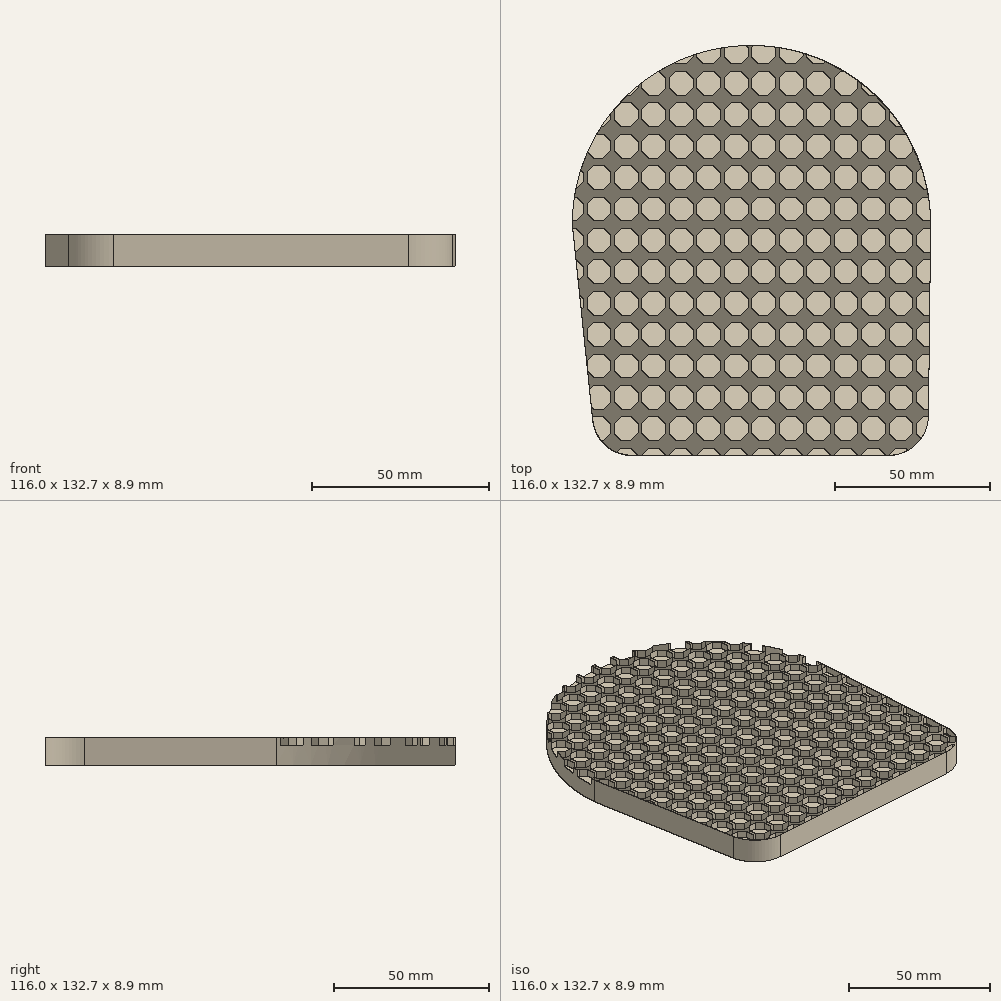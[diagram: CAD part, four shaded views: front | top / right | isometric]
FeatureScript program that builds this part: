
annotation { "Feature Type Name" : "Feature", "Feature Type Description" : "" }
export const myFeature = defineFeature(function(context is Context, id is Id, definition is map)
    precondition{}
    {
        {
            var Q0;
            Q0=qCreatedBy(makeId("Top.planeOp"),FACE);
            var sketch = newSketch(context, id + "F0", { "sketchPlane" : qUnion([Q0])});
            skLineSegment(sketch, "E0.0", {"start": v(-38.75, -61.92) * mm, "end": v(44.57, -61.92) * mm});
            skArc(sketch, "E1", {"start": v(57.99, 12.79) * mm, "mid": v(0, 70.77) * mm, "end": v(-57.99, 12.79) * mm});
            skLineSegment(sketch, "E2", {"start": v(-57.99, 12.79) * mm, "end": v(-51.38, -50.53) * mm});
            skLineSegment(sketch, "E3", {"start": v(57.99, 12.79) * mm, "end": v(57.27, -49.36) * mm});
            skArc(sketch, "E4.filletArc", {"start": v(-51.38, -50.53) * mm, "mid": v(-47.25, -58.65) * mm, "end": v(-38.75, -61.92) * mm});
            skArc(sketch, "E5.filletArc", {"start": v(44.57, -61.92) * mm, "mid": v(53.5, -58.25) * mm, "end": v(57.27, -49.36) * mm});
            skPoint(sketch, "E6.endSnap0", {"position": v(0, 70.77) * mm});
            skSolve(sketch);
        }
        {
            var Q0;
            Q0 = qSketchRegion(id + "F0", true);
            var Q1;
            Q1=makeQuery(id+"F0.imprint","IMPRINT",FACE,{"disambiguationData":[TD([[makeQuery(id+"F0.imprint","IMPRINT",EDGE,{"derivedFrom":sQuery(id+"F0.wireOp",EDGE,"E0.0")}),1.0]])]});
            extrude(context, id + "F1", {"entities" : qUnion([Q0, Q1]), "depth" : 6.35 * mm, "offsetDistance" : 25.4 * mm});
        }
        {
            var Q0;
            Q0=makeQuery(id+"F0.imprint","IMPRINT",FACE,{"disambiguationData":[TD([[makeQuery(id+"F0.imprint","IMPRINT",EDGE,{"derivedFrom":sQuery(id+"F0.wireOp",EDGE,"E0.0")}),1.0]])]});
            var sketch = newSketch(context, id + "F2", { "sketchPlane" : qUnion([Q0])});
            skLineSegment(sketch, "E7.1.5.2", {"start": v(-55.62, -9.87) * mm, "end": v(-54.45, -11.04) * mm});
            skLineSegment(sketch, "E7.1.5.4", {"start": v(-55.1, -14.87) * mm, "end": v(-54.45, -14.22) * mm});
            skLineSegment(sketch, "E7.1.5.5", {"start": v(-54.45, -14.22) * mm, "end": v(-54.45, -11.04) * mm});
            skLineSegment(sketch, "E7.1.6.2", {"start": v(-56.7, 1.36) * mm, "end": v(-54.45, -0.88) * mm});
            skLineSegment(sketch, "E7.1.6.3", {"start": v(-56.8, 1.36) * mm, "end": v(-56.7, 1.36) * mm});
            skLineSegment(sketch, "E7.1.6.4", {"start": v(-56.06, -5.67) * mm, "end": v(-54.45, -4.06) * mm});
            skLineSegment(sketch, "E7.1.6.5", {"start": v(-54.45, -4.06) * mm, "end": v(-54.45, -0.88) * mm});
            skLineSegment(sketch, "E7.1.7.0", {"start": v(-57.05, 3.86) * mm, "end": v(-56.7, 3.86) * mm});
            skLineSegment(sketch, "E7.1.7.2", {"start": v(-56.7, 11.52) * mm, "end": v(-54.45, 9.28) * mm});
            skLineSegment(sketch, "E7.1.7.3", {"start": v(-57.85, 11.52) * mm, "end": v(-56.7, 11.52) * mm});
            skLineSegment(sketch, "E7.1.7.4", {"start": v(-56.7, 3.86) * mm, "end": v(-54.45, 6.1) * mm});
            skLineSegment(sketch, "E7.1.7.5", {"start": v(-54.45, 6.1) * mm, "end": v(-54.45, 9.28) * mm});
            skLineSegment(sketch, "E7.1.8.0", {"start": v(-57.98, 14.02) * mm, "end": v(-56.7, 14.02) * mm});
            skLineSegment(sketch, "E7.1.8.2", {"start": v(-56.7, 21.68) * mm, "end": v(-54.45, 19.44) * mm});
            skLineSegment(sketch, "E7.1.8.3", {"start": v(-57.32, 21.68) * mm, "end": v(-56.7, 21.68) * mm});
            skLineSegment(sketch, "E7.1.8.4", {"start": v(-56.7, 14.02) * mm, "end": v(-54.45, 16.26) * mm});
            skLineSegment(sketch, "E7.1.8.5", {"start": v(-54.45, 16.26) * mm, "end": v(-54.45, 19.44) * mm});
            skLineSegment(sketch, "E7.1.9.0", {"start": v(-56.88, 24.18) * mm, "end": v(-56.7, 24.18) * mm});
            skLineSegment(sketch, "E7.1.9.2", {"start": v(-55.27, 30.42) * mm, "end": v(-54.45, 29.6) * mm});
            skLineSegment(sketch, "E7.1.9.4", {"start": v(-56.7, 24.18) * mm, "end": v(-54.45, 26.42) * mm});
            skLineSegment(sketch, "E7.1.9.5", {"start": v(-54.45, 26.42) * mm, "end": v(-54.45, 29.6) * mm});
            skLineSegment(sketch, "E7.2.1.0", {"start": v(-48.65, -57.1) * mm, "end": v(-47.8, -57.1) * mm});
            skLineSegment(sketch, "E7.2.1.1", {"start": v(-51.45, -49.9) * mm, "end": v(-50.98, -49.44) * mm});
            skLineSegment(sketch, "E7.2.1.2", {"start": v(-47.8, -49.44) * mm, "end": v(-45.56, -51.68) * mm});
            skLineSegment(sketch, "E7.2.1.3", {"start": v(-50.98, -49.44) * mm, "end": v(-47.8, -49.44) * mm});
            skLineSegment(sketch, "E7.2.1.4", {"start": v(-47.8, -57.1) * mm, "end": v(-45.56, -54.86) * mm});
            skLineSegment(sketch, "E7.2.1.5", {"start": v(-45.56, -54.86) * mm, "end": v(-45.56, -51.68) * mm});
            skLineSegment(sketch, "E7.2.2.0", {"start": v(-50.98, -46.94) * mm, "end": v(-47.8, -46.94) * mm});
            skLineSegment(sketch, "E7.2.2.1", {"start": v(-52.4, -40.7) * mm, "end": v(-50.98, -39.28) * mm});
            skLineSegment(sketch, "E7.2.2.2", {"start": v(-47.8, -39.28) * mm, "end": v(-45.56, -41.52) * mm});
            skLineSegment(sketch, "E7.2.2.3", {"start": v(-50.98, -39.28) * mm, "end": v(-47.8, -39.28) * mm});
            skLineSegment(sketch, "E7.2.2.4", {"start": v(-47.8, -46.94) * mm, "end": v(-45.56, -44.7) * mm});
            skLineSegment(sketch, "E7.2.2.5", {"start": v(-45.56, -44.7) * mm, "end": v(-45.56, -41.52) * mm});
            skLineSegment(sketch, "E7.2.2.6", {"start": v(-51.84, -46.07) * mm, "end": v(-50.98, -46.94) * mm});
            skLineSegment(sketch, "E7.2.3.0", {"start": v(-50.98, -36.78) * mm, "end": v(-47.8, -36.78) * mm});
            skLineSegment(sketch, "E7.2.3.1", {"start": v(-53.22, -31.36) * mm, "end": v(-50.98, -29.12) * mm});
            skLineSegment(sketch, "E7.2.3.2", {"start": v(-47.8, -29.12) * mm, "end": v(-45.56, -31.36) * mm});
            skLineSegment(sketch, "E7.2.3.3", {"start": v(-50.98, -29.12) * mm, "end": v(-47.8, -29.12) * mm});
            skLineSegment(sketch, "E7.2.3.4", {"start": v(-47.8, -36.78) * mm, "end": v(-45.56, -34.54) * mm});
            skLineSegment(sketch, "E7.2.3.5", {"start": v(-45.56, -34.54) * mm, "end": v(-45.56, -31.36) * mm});
            skLineSegment(sketch, "E7.2.3.6", {"start": v(-53.03, -34.73) * mm, "end": v(-50.98, -36.78) * mm});
            skLineSegment(sketch, "E7.2.3.7", {"start": v(-53.22, -32.86) * mm, "end": v(-53.22, -31.36) * mm});
            skLineSegment(sketch, "E7.2.4.0", {"start": v(-50.98, -26.62) * mm, "end": v(-47.8, -26.62) * mm});
            skLineSegment(sketch, "E7.2.4.1", {"start": v(-53.22, -21.2) * mm, "end": v(-50.98, -18.96) * mm});
            skLineSegment(sketch, "E7.2.4.2", {"start": v(-47.8, -18.96) * mm, "end": v(-45.56, -21.2) * mm});
            skLineSegment(sketch, "E7.2.4.3", {"start": v(-50.98, -18.96) * mm, "end": v(-47.8, -18.96) * mm});
            skLineSegment(sketch, "E7.2.4.4", {"start": v(-47.8, -26.62) * mm, "end": v(-45.56, -24.38) * mm});
            skLineSegment(sketch, "E7.2.4.5", {"start": v(-45.56, -24.38) * mm, "end": v(-45.56, -21.2) * mm});
            skLineSegment(sketch, "E7.2.4.6", {"start": v(-53.22, -24.38) * mm, "end": v(-50.98, -26.62) * mm});
            skLineSegment(sketch, "E7.2.4.7", {"start": v(-53.22, -24.38) * mm, "end": v(-53.22, -21.2) * mm});
            skLineSegment(sketch, "E7.2.5.0", {"start": v(-50.98, -16.46) * mm, "end": v(-47.8, -16.46) * mm});
            skLineSegment(sketch, "E7.2.5.1", {"start": v(-53.22, -11.04) * mm, "end": v(-50.98, -8.8) * mm});
            skLineSegment(sketch, "E7.2.5.2", {"start": v(-47.8, -8.8) * mm, "end": v(-45.56, -11.04) * mm});
            skLineSegment(sketch, "E7.2.5.3", {"start": v(-50.98, -8.8) * mm, "end": v(-47.8, -8.8) * mm});
            skLineSegment(sketch, "E7.2.5.4", {"start": v(-47.8, -16.46) * mm, "end": v(-45.56, -14.22) * mm});
            skLineSegment(sketch, "E7.2.5.5", {"start": v(-45.56, -14.22) * mm, "end": v(-45.56, -11.04) * mm});
            skLineSegment(sketch, "E7.2.5.6", {"start": v(-53.22, -14.22) * mm, "end": v(-50.98, -16.46) * mm});
            skLineSegment(sketch, "E7.2.5.7", {"start": v(-53.22, -14.22) * mm, "end": v(-53.22, -11.04) * mm});
            skLineSegment(sketch, "E7.2.6.0", {"start": v(-50.98, -6.3) * mm, "end": v(-47.8, -6.3) * mm});
            skLineSegment(sketch, "E7.2.6.1", {"start": v(-53.22, -0.88) * mm, "end": v(-50.98, 1.36) * mm});
            skLineSegment(sketch, "E7.2.6.2", {"start": v(-47.8, 1.36) * mm, "end": v(-45.56, -0.88) * mm});
            skLineSegment(sketch, "E7.2.6.3", {"start": v(-50.98, 1.36) * mm, "end": v(-47.8, 1.36) * mm});
            skLineSegment(sketch, "E7.2.6.4", {"start": v(-47.8, -6.3) * mm, "end": v(-45.56, -4.06) * mm});
            skLineSegment(sketch, "E7.2.6.5", {"start": v(-45.56, -4.06) * mm, "end": v(-45.56, -0.88) * mm});
            skLineSegment(sketch, "E7.2.6.6", {"start": v(-53.22, -4.06) * mm, "end": v(-50.98, -6.3) * mm});
            skLineSegment(sketch, "E7.2.6.7", {"start": v(-53.22, -4.06) * mm, "end": v(-53.22, -0.88) * mm});
            skLineSegment(sketch, "E7.2.7.0", {"start": v(-50.98, 3.86) * mm, "end": v(-47.8, 3.86) * mm});
            skLineSegment(sketch, "E7.2.7.1", {"start": v(-53.22, 9.28) * mm, "end": v(-50.98, 11.52) * mm});
            skLineSegment(sketch, "E7.2.7.2", {"start": v(-47.8, 11.52) * mm, "end": v(-45.56, 9.28) * mm});
            skLineSegment(sketch, "E7.2.7.3", {"start": v(-50.98, 11.52) * mm, "end": v(-47.8, 11.52) * mm});
            skLineSegment(sketch, "E7.2.7.4", {"start": v(-47.8, 3.86) * mm, "end": v(-45.56, 6.1) * mm});
            skLineSegment(sketch, "E7.2.7.5", {"start": v(-45.56, 6.1) * mm, "end": v(-45.56, 9.28) * mm});
            skLineSegment(sketch, "E7.2.7.6", {"start": v(-53.22, 6.1) * mm, "end": v(-50.98, 3.86) * mm});
            skLineSegment(sketch, "E7.2.7.7", {"start": v(-53.22, 6.1) * mm, "end": v(-53.22, 9.28) * mm});
            skLineSegment(sketch, "E7.2.8.0", {"start": v(-50.98, 14.02) * mm, "end": v(-47.8, 14.02) * mm});
            skLineSegment(sketch, "E7.2.8.1", {"start": v(-53.22, 19.44) * mm, "end": v(-50.98, 21.68) * mm});
            skLineSegment(sketch, "E7.2.8.2", {"start": v(-47.8, 21.68) * mm, "end": v(-45.56, 19.44) * mm});
            skLineSegment(sketch, "E7.2.8.3", {"start": v(-50.98, 21.68) * mm, "end": v(-47.8, 21.68) * mm});
            skLineSegment(sketch, "E7.2.8.4", {"start": v(-47.8, 14.02) * mm, "end": v(-45.56, 16.26) * mm});
            skLineSegment(sketch, "E7.2.8.5", {"start": v(-45.56, 16.26) * mm, "end": v(-45.56, 19.44) * mm});
            skLineSegment(sketch, "E7.2.8.6", {"start": v(-53.22, 16.26) * mm, "end": v(-50.98, 14.02) * mm});
            skLineSegment(sketch, "E7.2.8.7", {"start": v(-53.22, 16.26) * mm, "end": v(-53.22, 19.44) * mm});
            skLineSegment(sketch, "E7.2.9.0", {"start": v(-50.98, 24.18) * mm, "end": v(-47.8, 24.18) * mm});
            skLineSegment(sketch, "E7.2.9.1", {"start": v(-53.22, 29.6) * mm, "end": v(-50.98, 31.84) * mm});
            skLineSegment(sketch, "E7.2.9.2", {"start": v(-47.8, 31.84) * mm, "end": v(-45.56, 29.6) * mm});
            skLineSegment(sketch, "E7.2.9.3", {"start": v(-50.98, 31.84) * mm, "end": v(-47.8, 31.84) * mm});
            skLineSegment(sketch, "E7.2.9.4", {"start": v(-47.8, 24.18) * mm, "end": v(-45.56, 26.42) * mm});
            skLineSegment(sketch, "E7.2.9.5", {"start": v(-45.56, 26.42) * mm, "end": v(-45.56, 29.6) * mm});
            skLineSegment(sketch, "E7.2.9.6", {"start": v(-53.22, 26.42) * mm, "end": v(-50.98, 24.18) * mm});
            skLineSegment(sketch, "E7.2.9.7", {"start": v(-53.22, 26.42) * mm, "end": v(-53.22, 29.6) * mm});
            skLineSegment(sketch, "E7.2.10.0", {"start": v(-50.98, 34.34) * mm, "end": v(-47.8, 34.34) * mm});
            skLineSegment(sketch, "E7.2.10.2", {"start": v(-47.8, 42) * mm, "end": v(-45.56, 39.76) * mm});
            skLineSegment(sketch, "E7.2.10.3", {"start": v(-50.14, 42) * mm, "end": v(-47.8, 42) * mm});
            skLineSegment(sketch, "E7.2.10.4", {"start": v(-47.8, 34.34) * mm, "end": v(-45.56, 36.58) * mm});
            skLineSegment(sketch, "E7.2.10.5", {"start": v(-45.56, 36.58) * mm, "end": v(-45.56, 39.76) * mm});
            skLineSegment(sketch, "E7.2.10.6", {"start": v(-53.01, 36.37) * mm, "end": v(-50.98, 34.34) * mm});
            skLineSegment(sketch, "E7.2.11.0", {"start": v(-48.6, 44.5) * mm, "end": v(-47.8, 44.5) * mm});
            skLineSegment(sketch, "E7.2.11.4", {"start": v(-47.8, 44.5) * mm, "end": v(-45.56, 46.74) * mm});
            skLineSegment(sketch, "E7.2.11.5", {"start": v(-45.56, 46.74) * mm, "end": v(-45.56, 48.74) * mm});
            skLineSegment(sketch, "E7.3.0.1", {"start": v(-43.44, -60.95) * mm, "end": v(-42.09, -59.6) * mm});
            skLineSegment(sketch, "E7.3.0.2", {"start": v(-38.91, -59.6) * mm, "end": v(-36.67, -61.84) * mm});
            skLineSegment(sketch, "E7.3.0.3", {"start": v(-42.09, -59.6) * mm, "end": v(-38.91, -59.6) * mm});
            skLineSegment(sketch, "E7.3.1.0", {"start": v(-42.09, -57.1) * mm, "end": v(-38.91, -57.1) * mm});
            skLineSegment(sketch, "E7.3.1.1", {"start": v(-44.33, -51.68) * mm, "end": v(-42.09, -49.44) * mm});
            skLineSegment(sketch, "E7.3.1.2", {"start": v(-38.91, -49.44) * mm, "end": v(-36.67, -51.68) * mm});
            skLineSegment(sketch, "E7.3.1.3", {"start": v(-42.09, -49.44) * mm, "end": v(-38.91, -49.44) * mm});
            skLineSegment(sketch, "E7.3.1.4", {"start": v(-38.91, -57.1) * mm, "end": v(-36.67, -54.86) * mm});
            skLineSegment(sketch, "E7.3.1.5", {"start": v(-36.67, -54.86) * mm, "end": v(-36.67, -51.68) * mm});
            skLineSegment(sketch, "E7.3.1.6", {"start": v(-44.33, -54.86) * mm, "end": v(-42.09, -57.1) * mm});
            skLineSegment(sketch, "E7.3.1.7", {"start": v(-44.33, -54.86) * mm, "end": v(-44.33, -51.68) * mm});
            skLineSegment(sketch, "E7.3.2.0", {"start": v(-42.09, -46.94) * mm, "end": v(-38.91, -46.94) * mm});
            skLineSegment(sketch, "E7.3.2.1", {"start": v(-44.33, -41.52) * mm, "end": v(-42.09, -39.28) * mm});
            skLineSegment(sketch, "E7.3.2.2", {"start": v(-38.91, -39.28) * mm, "end": v(-36.67, -41.52) * mm});
            skLineSegment(sketch, "E7.3.2.3", {"start": v(-42.09, -39.28) * mm, "end": v(-38.91, -39.28) * mm});
            skLineSegment(sketch, "E7.3.2.4", {"start": v(-38.91, -46.94) * mm, "end": v(-36.67, -44.7) * mm});
            skLineSegment(sketch, "E7.3.2.5", {"start": v(-36.67, -44.7) * mm, "end": v(-36.67, -41.52) * mm});
            skLineSegment(sketch, "E7.3.2.6", {"start": v(-44.33, -44.7) * mm, "end": v(-42.09, -46.94) * mm});
            skLineSegment(sketch, "E7.3.2.7", {"start": v(-44.33, -44.7) * mm, "end": v(-44.33, -41.52) * mm});
            skLineSegment(sketch, "E7.3.3.0", {"start": v(-42.09, -36.78) * mm, "end": v(-38.91, -36.78) * mm});
            skLineSegment(sketch, "E7.3.3.1", {"start": v(-44.33, -31.36) * mm, "end": v(-42.09, -29.12) * mm});
            skLineSegment(sketch, "E7.3.3.2", {"start": v(-38.91, -29.12) * mm, "end": v(-36.67, -31.36) * mm});
            skLineSegment(sketch, "E7.3.3.3", {"start": v(-42.09, -29.12) * mm, "end": v(-38.91, -29.12) * mm});
            skLineSegment(sketch, "E7.3.3.4", {"start": v(-38.91, -36.78) * mm, "end": v(-36.67, -34.54) * mm});
            skLineSegment(sketch, "E7.3.3.5", {"start": v(-36.67, -34.54) * mm, "end": v(-36.67, -31.36) * mm});
            skLineSegment(sketch, "E7.3.3.6", {"start": v(-44.33, -34.54) * mm, "end": v(-42.09, -36.78) * mm});
            skLineSegment(sketch, "E7.3.3.7", {"start": v(-44.33, -34.54) * mm, "end": v(-44.33, -31.36) * mm});
            skLineSegment(sketch, "E7.3.4.0", {"start": v(-42.09, -26.62) * mm, "end": v(-38.91, -26.62) * mm});
            skLineSegment(sketch, "E7.3.4.1", {"start": v(-44.33, -21.2) * mm, "end": v(-42.09, -18.96) * mm});
            skLineSegment(sketch, "E7.3.4.2", {"start": v(-38.91, -18.96) * mm, "end": v(-36.67, -21.2) * mm});
            skLineSegment(sketch, "E7.3.4.3", {"start": v(-42.09, -18.96) * mm, "end": v(-38.91, -18.96) * mm});
            skLineSegment(sketch, "E7.3.4.4", {"start": v(-38.91, -26.62) * mm, "end": v(-36.67, -24.38) * mm});
            skLineSegment(sketch, "E7.3.4.5", {"start": v(-36.67, -24.38) * mm, "end": v(-36.67, -21.2) * mm});
            skLineSegment(sketch, "E7.3.4.6", {"start": v(-44.33, -24.38) * mm, "end": v(-42.09, -26.62) * mm});
            skLineSegment(sketch, "E7.3.4.7", {"start": v(-44.33, -24.38) * mm, "end": v(-44.33, -21.2) * mm});
            skLineSegment(sketch, "E7.3.5.0", {"start": v(-42.09, -16.46) * mm, "end": v(-38.91, -16.46) * mm});
            skLineSegment(sketch, "E7.3.5.1", {"start": v(-44.33, -11.04) * mm, "end": v(-42.09, -8.8) * mm});
            skLineSegment(sketch, "E7.3.5.2", {"start": v(-38.91, -8.8) * mm, "end": v(-36.67, -11.04) * mm});
            skLineSegment(sketch, "E7.3.5.3", {"start": v(-42.09, -8.8) * mm, "end": v(-38.91, -8.8) * mm});
            skLineSegment(sketch, "E7.3.5.4", {"start": v(-38.91, -16.46) * mm, "end": v(-36.67, -14.22) * mm});
            skLineSegment(sketch, "E7.3.5.5", {"start": v(-36.67, -14.22) * mm, "end": v(-36.67, -11.04) * mm});
            skLineSegment(sketch, "E7.3.5.6", {"start": v(-44.33, -14.22) * mm, "end": v(-42.09, -16.46) * mm});
            skLineSegment(sketch, "E7.3.5.7", {"start": v(-44.33, -14.22) * mm, "end": v(-44.33, -11.04) * mm});
            skLineSegment(sketch, "E7.3.6.0", {"start": v(-42.09, -6.3) * mm, "end": v(-38.91, -6.3) * mm});
            skLineSegment(sketch, "E7.3.6.1", {"start": v(-44.33, -0.88) * mm, "end": v(-42.09, 1.36) * mm});
            skLineSegment(sketch, "E7.3.6.2", {"start": v(-38.91, 1.36) * mm, "end": v(-36.67, -0.88) * mm});
            skLineSegment(sketch, "E7.3.6.3", {"start": v(-42.09, 1.36) * mm, "end": v(-38.91, 1.36) * mm});
            skLineSegment(sketch, "E7.3.6.4", {"start": v(-38.91, -6.3) * mm, "end": v(-36.67, -4.06) * mm});
            skLineSegment(sketch, "E7.3.6.5", {"start": v(-36.67, -4.06) * mm, "end": v(-36.67, -0.88) * mm});
            skLineSegment(sketch, "E7.3.6.6", {"start": v(-44.33, -4.06) * mm, "end": v(-42.09, -6.3) * mm});
            skLineSegment(sketch, "E7.3.6.7", {"start": v(-44.33, -4.06) * mm, "end": v(-44.33, -0.88) * mm});
            skLineSegment(sketch, "E7.3.7.0", {"start": v(-42.09, 3.86) * mm, "end": v(-38.91, 3.86) * mm});
            skLineSegment(sketch, "E7.3.7.1", {"start": v(-44.33, 9.28) * mm, "end": v(-42.09, 11.52) * mm});
            skLineSegment(sketch, "E7.3.7.2", {"start": v(-38.91, 11.52) * mm, "end": v(-36.67, 9.28) * mm});
            skLineSegment(sketch, "E7.3.7.3", {"start": v(-42.09, 11.52) * mm, "end": v(-38.91, 11.52) * mm});
            skLineSegment(sketch, "E7.3.7.4", {"start": v(-38.91, 3.86) * mm, "end": v(-36.67, 6.1) * mm});
            skLineSegment(sketch, "E7.3.7.5", {"start": v(-36.67, 6.1) * mm, "end": v(-36.67, 9.28) * mm});
            skLineSegment(sketch, "E7.3.7.6", {"start": v(-44.33, 6.1) * mm, "end": v(-42.09, 3.86) * mm});
            skLineSegment(sketch, "E7.3.7.7", {"start": v(-44.33, 6.1) * mm, "end": v(-44.33, 9.28) * mm});
            skLineSegment(sketch, "E7.3.8.0", {"start": v(-42.09, 14.02) * mm, "end": v(-38.91, 14.02) * mm});
            skLineSegment(sketch, "E7.3.8.1", {"start": v(-44.33, 19.44) * mm, "end": v(-42.09, 21.68) * mm});
            skLineSegment(sketch, "E7.3.8.2", {"start": v(-38.91, 21.68) * mm, "end": v(-36.67, 19.44) * mm});
            skLineSegment(sketch, "E7.3.8.3", {"start": v(-42.09, 21.68) * mm, "end": v(-38.91, 21.68) * mm});
            skLineSegment(sketch, "E7.3.8.4", {"start": v(-38.91, 14.02) * mm, "end": v(-36.67, 16.26) * mm});
            skLineSegment(sketch, "E7.3.8.5", {"start": v(-36.67, 16.26) * mm, "end": v(-36.67, 19.44) * mm});
            skLineSegment(sketch, "E7.3.8.6", {"start": v(-44.33, 16.26) * mm, "end": v(-42.09, 14.02) * mm});
            skLineSegment(sketch, "E7.3.8.7", {"start": v(-44.33, 16.26) * mm, "end": v(-44.33, 19.44) * mm});
            skLineSegment(sketch, "E7.3.9.0", {"start": v(-42.09, 24.18) * mm, "end": v(-38.91, 24.18) * mm});
            skLineSegment(sketch, "E7.3.9.1", {"start": v(-44.33, 29.6) * mm, "end": v(-42.09, 31.84) * mm});
            skLineSegment(sketch, "E7.3.9.2", {"start": v(-38.91, 31.84) * mm, "end": v(-36.67, 29.6) * mm});
            skLineSegment(sketch, "E7.3.9.3", {"start": v(-42.09, 31.84) * mm, "end": v(-38.91, 31.84) * mm});
            skLineSegment(sketch, "E7.3.9.4", {"start": v(-38.91, 24.18) * mm, "end": v(-36.67, 26.42) * mm});
            skLineSegment(sketch, "E7.3.9.5", {"start": v(-36.67, 26.42) * mm, "end": v(-36.67, 29.6) * mm});
            skLineSegment(sketch, "E7.3.9.6", {"start": v(-44.33, 26.42) * mm, "end": v(-42.09, 24.18) * mm});
            skLineSegment(sketch, "E7.3.9.7", {"start": v(-44.33, 26.42) * mm, "end": v(-44.33, 29.6) * mm});
            skLineSegment(sketch, "E7.3.10.0", {"start": v(-42.09, 34.34) * mm, "end": v(-38.91, 34.34) * mm});
            skLineSegment(sketch, "E7.3.10.1", {"start": v(-44.33, 39.76) * mm, "end": v(-42.09, 42) * mm});
            skLineSegment(sketch, "E7.3.10.2", {"start": v(-38.91, 42) * mm, "end": v(-36.67, 39.76) * mm});
            skLineSegment(sketch, "E7.3.10.3", {"start": v(-42.09, 42) * mm, "end": v(-38.91, 42) * mm});
            skLineSegment(sketch, "E7.3.10.4", {"start": v(-38.91, 34.34) * mm, "end": v(-36.67, 36.58) * mm});
            skLineSegment(sketch, "E7.3.10.5", {"start": v(-36.67, 36.58) * mm, "end": v(-36.67, 39.76) * mm});
            skLineSegment(sketch, "E7.3.10.6", {"start": v(-44.33, 36.58) * mm, "end": v(-42.09, 34.34) * mm});
            skLineSegment(sketch, "E7.3.10.7", {"start": v(-44.33, 36.58) * mm, "end": v(-44.33, 39.76) * mm});
            skLineSegment(sketch, "E7.3.11.0", {"start": v(-42.09, 44.5) * mm, "end": v(-38.91, 44.5) * mm});
            skLineSegment(sketch, "E7.3.11.1", {"start": v(-44.33, 49.92) * mm, "end": v(-42.09, 52.16) * mm});
            skLineSegment(sketch, "E7.3.11.2", {"start": v(-38.91, 52.16) * mm, "end": v(-36.67, 49.92) * mm});
            skLineSegment(sketch, "E7.3.11.3", {"start": v(-42.09, 52.16) * mm, "end": v(-38.91, 52.16) * mm});
            skLineSegment(sketch, "E7.3.11.4", {"start": v(-38.91, 44.5) * mm, "end": v(-36.67, 46.74) * mm});
            skLineSegment(sketch, "E7.3.11.5", {"start": v(-36.67, 46.74) * mm, "end": v(-36.67, 49.92) * mm});
            skLineSegment(sketch, "E7.3.11.6", {"start": v(-44.33, 46.74) * mm, "end": v(-42.09, 44.5) * mm});
            skLineSegment(sketch, "E7.3.11.7", {"start": v(-44.33, 46.74) * mm, "end": v(-44.33, 49.92) * mm});
            skLineSegment(sketch, "E7.3.12.0", {"start": v(-40.2, 54.66) * mm, "end": v(-38.91, 54.66) * mm});
            skLineSegment(sketch, "E7.3.12.4", {"start": v(-38.91, 54.66) * mm, "end": v(-36.67, 56.9) * mm});
            skLineSegment(sketch, "E7.3.12.5", {"start": v(-36.67, 56.9) * mm, "end": v(-36.67, 57.79) * mm});
            skLineSegment(sketch, "E7.4.0.1", {"start": v(-35.44, -61.84) * mm, "end": v(-33.2, -59.6) * mm});
            skLineSegment(sketch, "E7.4.0.2", {"start": v(-30.02, -59.6) * mm, "end": v(-27.78, -61.84) * mm});
            skLineSegment(sketch, "E7.4.0.3", {"start": v(-33.2, -59.6) * mm, "end": v(-30.02, -59.6) * mm});
            skLineSegment(sketch, "E7.4.1.0", {"start": v(-33.2, -57.1) * mm, "end": v(-30.02, -57.1) * mm});
            skLineSegment(sketch, "E7.4.1.1", {"start": v(-35.44, -51.68) * mm, "end": v(-33.2, -49.44) * mm});
            skLineSegment(sketch, "E7.4.1.2", {"start": v(-30.02, -49.44) * mm, "end": v(-27.78, -51.68) * mm});
            skLineSegment(sketch, "E7.4.1.3", {"start": v(-33.2, -49.44) * mm, "end": v(-30.02, -49.44) * mm});
            skLineSegment(sketch, "E7.4.1.4", {"start": v(-30.02, -57.1) * mm, "end": v(-27.78, -54.86) * mm});
            skLineSegment(sketch, "E7.4.1.5", {"start": v(-27.78, -54.86) * mm, "end": v(-27.78, -51.68) * mm});
            skLineSegment(sketch, "E7.4.1.6", {"start": v(-35.44, -54.86) * mm, "end": v(-33.2, -57.1) * mm});
            skLineSegment(sketch, "E7.4.1.7", {"start": v(-35.44, -54.86) * mm, "end": v(-35.44, -51.68) * mm});
            skLineSegment(sketch, "E7.4.2.0", {"start": v(-33.2, -46.94) * mm, "end": v(-30.02, -46.94) * mm});
            skLineSegment(sketch, "E7.4.2.1", {"start": v(-35.44, -41.52) * mm, "end": v(-33.2, -39.28) * mm});
            skLineSegment(sketch, "E7.4.2.2", {"start": v(-30.02, -39.28) * mm, "end": v(-27.78, -41.52) * mm});
            skLineSegment(sketch, "E7.4.2.3", {"start": v(-33.2, -39.28) * mm, "end": v(-30.02, -39.28) * mm});
            skLineSegment(sketch, "E7.4.2.4", {"start": v(-30.02, -46.94) * mm, "end": v(-27.78, -44.7) * mm});
            skLineSegment(sketch, "E7.4.2.5", {"start": v(-27.78, -44.7) * mm, "end": v(-27.78, -41.52) * mm});
            skLineSegment(sketch, "E7.4.2.6", {"start": v(-35.44, -44.7) * mm, "end": v(-33.2, -46.94) * mm});
            skLineSegment(sketch, "E7.4.2.7", {"start": v(-35.44, -44.7) * mm, "end": v(-35.44, -41.52) * mm});
            skLineSegment(sketch, "E7.4.3.0", {"start": v(-33.2, -36.78) * mm, "end": v(-30.02, -36.78) * mm});
            skLineSegment(sketch, "E7.4.3.1", {"start": v(-35.44, -31.36) * mm, "end": v(-33.2, -29.12) * mm});
            skLineSegment(sketch, "E7.4.3.2", {"start": v(-30.02, -29.12) * mm, "end": v(-27.78, -31.36) * mm});
            skLineSegment(sketch, "E7.4.3.3", {"start": v(-33.2, -29.12) * mm, "end": v(-30.02, -29.12) * mm});
            skLineSegment(sketch, "E7.4.3.4", {"start": v(-30.02, -36.78) * mm, "end": v(-27.78, -34.54) * mm});
            skLineSegment(sketch, "E7.4.3.5", {"start": v(-27.78, -34.54) * mm, "end": v(-27.78, -31.36) * mm});
            skLineSegment(sketch, "E7.4.3.6", {"start": v(-35.44, -34.54) * mm, "end": v(-33.2, -36.78) * mm});
            skLineSegment(sketch, "E7.4.3.7", {"start": v(-35.44, -34.54) * mm, "end": v(-35.44, -31.36) * mm});
            skLineSegment(sketch, "E7.4.4.0", {"start": v(-33.2, -26.62) * mm, "end": v(-30.02, -26.62) * mm});
            skLineSegment(sketch, "E7.4.4.1", {"start": v(-35.44, -21.2) * mm, "end": v(-33.2, -18.96) * mm});
            skLineSegment(sketch, "E7.4.4.2", {"start": v(-30.02, -18.96) * mm, "end": v(-27.78, -21.2) * mm});
            skLineSegment(sketch, "E7.4.4.3", {"start": v(-33.2, -18.96) * mm, "end": v(-30.02, -18.96) * mm});
            skLineSegment(sketch, "E7.4.4.4", {"start": v(-30.02, -26.62) * mm, "end": v(-27.78, -24.38) * mm});
            skLineSegment(sketch, "E7.4.4.5", {"start": v(-27.78, -24.38) * mm, "end": v(-27.78, -21.2) * mm});
            skLineSegment(sketch, "E7.4.4.6", {"start": v(-35.44, -24.38) * mm, "end": v(-33.2, -26.62) * mm});
            skLineSegment(sketch, "E7.4.4.7", {"start": v(-35.44, -24.38) * mm, "end": v(-35.44, -21.2) * mm});
            skLineSegment(sketch, "E7.4.5.0", {"start": v(-33.2, -16.46) * mm, "end": v(-30.02, -16.46) * mm});
            skLineSegment(sketch, "E7.4.5.1", {"start": v(-35.44, -11.04) * mm, "end": v(-33.2, -8.8) * mm});
            skLineSegment(sketch, "E7.4.5.2", {"start": v(-30.02, -8.8) * mm, "end": v(-27.78, -11.04) * mm});
            skLineSegment(sketch, "E7.4.5.3", {"start": v(-33.2, -8.8) * mm, "end": v(-30.02, -8.8) * mm});
            skLineSegment(sketch, "E7.4.5.4", {"start": v(-30.02, -16.46) * mm, "end": v(-27.78, -14.22) * mm});
            skLineSegment(sketch, "E7.4.5.5", {"start": v(-27.78, -14.22) * mm, "end": v(-27.78, -11.04) * mm});
            skLineSegment(sketch, "E7.4.5.6", {"start": v(-35.44, -14.22) * mm, "end": v(-33.2, -16.46) * mm});
            skLineSegment(sketch, "E7.4.5.7", {"start": v(-35.44, -14.22) * mm, "end": v(-35.44, -11.04) * mm});
            skLineSegment(sketch, "E7.4.6.0", {"start": v(-33.2, -6.3) * mm, "end": v(-30.02, -6.3) * mm});
            skLineSegment(sketch, "E7.4.6.1", {"start": v(-35.44, -0.88) * mm, "end": v(-33.2, 1.36) * mm});
            skLineSegment(sketch, "E7.4.6.2", {"start": v(-30.02, 1.36) * mm, "end": v(-27.78, -0.88) * mm});
            skLineSegment(sketch, "E7.4.6.3", {"start": v(-33.2, 1.36) * mm, "end": v(-30.02, 1.36) * mm});
            skLineSegment(sketch, "E7.4.6.4", {"start": v(-30.02, -6.3) * mm, "end": v(-27.78, -4.06) * mm});
            skLineSegment(sketch, "E7.4.6.5", {"start": v(-27.78, -4.06) * mm, "end": v(-27.78, -0.88) * mm});
            skLineSegment(sketch, "E7.4.6.6", {"start": v(-35.44, -4.06) * mm, "end": v(-33.2, -6.3) * mm});
            skLineSegment(sketch, "E7.4.6.7", {"start": v(-35.44, -4.06) * mm, "end": v(-35.44, -0.88) * mm});
            skLineSegment(sketch, "E7.4.7.0", {"start": v(-33.2, 3.86) * mm, "end": v(-30.02, 3.86) * mm});
            skLineSegment(sketch, "E7.4.7.1", {"start": v(-35.44, 9.28) * mm, "end": v(-33.2, 11.52) * mm});
            skLineSegment(sketch, "E7.4.7.2", {"start": v(-30.02, 11.52) * mm, "end": v(-27.78, 9.28) * mm});
            skLineSegment(sketch, "E7.4.7.3", {"start": v(-33.2, 11.52) * mm, "end": v(-30.02, 11.52) * mm});
            skLineSegment(sketch, "E7.4.7.4", {"start": v(-30.02, 3.86) * mm, "end": v(-27.78, 6.1) * mm});
            skLineSegment(sketch, "E7.4.7.5", {"start": v(-27.78, 6.1) * mm, "end": v(-27.78, 9.28) * mm});
            skLineSegment(sketch, "E7.4.7.6", {"start": v(-35.44, 6.1) * mm, "end": v(-33.2, 3.86) * mm});
            skLineSegment(sketch, "E7.4.7.7", {"start": v(-35.44, 6.1) * mm, "end": v(-35.44, 9.28) * mm});
            skLineSegment(sketch, "E7.4.8.0", {"start": v(-33.2, 14.02) * mm, "end": v(-30.02, 14.02) * mm});
            skLineSegment(sketch, "E7.4.8.1", {"start": v(-35.44, 19.44) * mm, "end": v(-33.2, 21.68) * mm});
            skLineSegment(sketch, "E7.4.8.2", {"start": v(-30.02, 21.68) * mm, "end": v(-27.78, 19.44) * mm});
            skLineSegment(sketch, "E7.4.8.3", {"start": v(-33.2, 21.68) * mm, "end": v(-30.02, 21.68) * mm});
            skLineSegment(sketch, "E7.4.8.4", {"start": v(-30.02, 14.02) * mm, "end": v(-27.78, 16.26) * mm});
            skLineSegment(sketch, "E7.4.8.5", {"start": v(-27.78, 16.26) * mm, "end": v(-27.78, 19.44) * mm});
            skLineSegment(sketch, "E7.4.8.6", {"start": v(-35.44, 16.26) * mm, "end": v(-33.2, 14.02) * mm});
            skLineSegment(sketch, "E7.4.8.7", {"start": v(-35.44, 16.26) * mm, "end": v(-35.44, 19.44) * mm});
            skLineSegment(sketch, "E7.4.9.0", {"start": v(-33.2, 24.18) * mm, "end": v(-30.02, 24.18) * mm});
            skLineSegment(sketch, "E7.4.9.1", {"start": v(-35.44, 29.6) * mm, "end": v(-33.2, 31.84) * mm});
            skLineSegment(sketch, "E7.4.9.2", {"start": v(-30.02, 31.84) * mm, "end": v(-27.78, 29.6) * mm});
            skLineSegment(sketch, "E7.4.9.3", {"start": v(-33.2, 31.84) * mm, "end": v(-30.02, 31.84) * mm});
            skLineSegment(sketch, "E7.4.9.4", {"start": v(-30.02, 24.18) * mm, "end": v(-27.78, 26.42) * mm});
            skLineSegment(sketch, "E7.4.9.5", {"start": v(-27.78, 26.42) * mm, "end": v(-27.78, 29.6) * mm});
            skLineSegment(sketch, "E7.4.9.6", {"start": v(-35.44, 26.42) * mm, "end": v(-33.2, 24.18) * mm});
            skLineSegment(sketch, "E7.4.9.7", {"start": v(-35.44, 26.42) * mm, "end": v(-35.44, 29.6) * mm});
            skLineSegment(sketch, "E7.4.10.0", {"start": v(-33.2, 34.34) * mm, "end": v(-30.02, 34.34) * mm});
            skLineSegment(sketch, "E7.4.10.1", {"start": v(-35.44, 39.76) * mm, "end": v(-33.2, 42) * mm});
            skLineSegment(sketch, "E7.4.10.2", {"start": v(-30.02, 42) * mm, "end": v(-27.78, 39.76) * mm});
            skLineSegment(sketch, "E7.4.10.3", {"start": v(-33.2, 42) * mm, "end": v(-30.02, 42) * mm});
            skLineSegment(sketch, "E7.4.10.4", {"start": v(-30.02, 34.34) * mm, "end": v(-27.78, 36.58) * mm});
            skLineSegment(sketch, "E7.4.10.5", {"start": v(-27.78, 36.58) * mm, "end": v(-27.78, 39.76) * mm});
            skLineSegment(sketch, "E7.4.10.6", {"start": v(-35.44, 36.58) * mm, "end": v(-33.2, 34.34) * mm});
            skLineSegment(sketch, "E7.4.10.7", {"start": v(-35.44, 36.58) * mm, "end": v(-35.44, 39.76) * mm});
            skLineSegment(sketch, "E7.4.11.0", {"start": v(-33.2, 44.5) * mm, "end": v(-30.02, 44.5) * mm});
            skLineSegment(sketch, "E7.4.11.1", {"start": v(-35.44, 49.92) * mm, "end": v(-33.2, 52.16) * mm});
            skLineSegment(sketch, "E7.4.11.2", {"start": v(-30.02, 52.16) * mm, "end": v(-27.78, 49.92) * mm});
            skLineSegment(sketch, "E7.4.11.3", {"start": v(-33.2, 52.16) * mm, "end": v(-30.02, 52.16) * mm});
            skLineSegment(sketch, "E7.4.11.4", {"start": v(-30.02, 44.5) * mm, "end": v(-27.78, 46.74) * mm});
            skLineSegment(sketch, "E7.4.11.5", {"start": v(-27.78, 46.74) * mm, "end": v(-27.78, 49.92) * mm});
            skLineSegment(sketch, "E7.4.11.6", {"start": v(-35.44, 46.74) * mm, "end": v(-33.2, 44.5) * mm});
            skLineSegment(sketch, "E7.4.11.7", {"start": v(-35.44, 46.74) * mm, "end": v(-35.44, 49.92) * mm});
            skLineSegment(sketch, "E7.4.12.0", {"start": v(-33.2, 54.66) * mm, "end": v(-30.02, 54.66) * mm});
            skLineSegment(sketch, "E7.4.12.2", {"start": v(-30.02, 62.32) * mm, "end": v(-27.78, 60.08) * mm});
            skLineSegment(sketch, "E7.4.12.3", {"start": v(-30.27, 62.32) * mm, "end": v(-30.02, 62.32) * mm});
            skLineSegment(sketch, "E7.4.12.4", {"start": v(-30.02, 54.66) * mm, "end": v(-27.78, 56.9) * mm});
            skLineSegment(sketch, "E7.4.12.5", {"start": v(-27.78, 56.9) * mm, "end": v(-27.78, 60.08) * mm});
            skLineSegment(sketch, "E7.4.12.6", {"start": v(-35.44, 56.9) * mm, "end": v(-33.2, 54.66) * mm});
            skLineSegment(sketch, "E7.4.12.7", {"start": v(-35.44, 56.9) * mm, "end": v(-35.44, 58.76) * mm});
            skLineSegment(sketch, "E7.5.0.1", {"start": v(-26.55, -61.84) * mm, "end": v(-24.3, -59.6) * mm});
            skLineSegment(sketch, "E7.5.0.2", {"start": v(-21.13, -59.6) * mm, "end": v(-18.89, -61.84) * mm});
            skLineSegment(sketch, "E7.5.0.3", {"start": v(-24.3, -59.6) * mm, "end": v(-21.13, -59.6) * mm});
            skLineSegment(sketch, "E7.5.1.0", {"start": v(-24.3, -57.1) * mm, "end": v(-21.13, -57.1) * mm});
            skLineSegment(sketch, "E7.5.1.1", {"start": v(-26.55, -51.68) * mm, "end": v(-24.3, -49.44) * mm});
            skLineSegment(sketch, "E7.5.1.2", {"start": v(-21.13, -49.44) * mm, "end": v(-18.89, -51.68) * mm});
            skLineSegment(sketch, "E7.5.1.3", {"start": v(-24.3, -49.44) * mm, "end": v(-21.13, -49.44) * mm});
            skLineSegment(sketch, "E7.5.1.4", {"start": v(-21.13, -57.1) * mm, "end": v(-18.89, -54.86) * mm});
            skLineSegment(sketch, "E7.5.1.5", {"start": v(-18.89, -54.86) * mm, "end": v(-18.89, -51.68) * mm});
            skLineSegment(sketch, "E7.5.1.6", {"start": v(-26.55, -54.86) * mm, "end": v(-24.3, -57.1) * mm});
            skLineSegment(sketch, "E7.5.1.7", {"start": v(-26.55, -54.86) * mm, "end": v(-26.55, -51.68) * mm});
            skLineSegment(sketch, "E7.5.2.0", {"start": v(-24.3, -46.94) * mm, "end": v(-21.13, -46.94) * mm});
            skLineSegment(sketch, "E7.5.2.1", {"start": v(-26.55, -41.52) * mm, "end": v(-24.3, -39.28) * mm});
            skLineSegment(sketch, "E7.5.2.2", {"start": v(-21.13, -39.28) * mm, "end": v(-18.89, -41.52) * mm});
            skLineSegment(sketch, "E7.5.2.3", {"start": v(-24.3, -39.28) * mm, "end": v(-21.13, -39.28) * mm});
            skLineSegment(sketch, "E7.5.2.4", {"start": v(-21.13, -46.94) * mm, "end": v(-18.89, -44.7) * mm});
            skLineSegment(sketch, "E7.5.2.5", {"start": v(-18.89, -44.7) * mm, "end": v(-18.89, -41.52) * mm});
            skLineSegment(sketch, "E7.5.2.6", {"start": v(-26.55, -44.7) * mm, "end": v(-24.3, -46.94) * mm});
            skLineSegment(sketch, "E7.5.2.7", {"start": v(-26.55, -44.7) * mm, "end": v(-26.55, -41.52) * mm});
            skLineSegment(sketch, "E7.5.3.0", {"start": v(-24.3, -36.78) * mm, "end": v(-21.13, -36.78) * mm});
            skLineSegment(sketch, "E7.5.3.1", {"start": v(-26.55, -31.36) * mm, "end": v(-24.3, -29.12) * mm});
            skLineSegment(sketch, "E7.5.3.2", {"start": v(-21.13, -29.12) * mm, "end": v(-18.89, -31.36) * mm});
            skLineSegment(sketch, "E7.5.3.3", {"start": v(-24.3, -29.12) * mm, "end": v(-21.13, -29.12) * mm});
            skLineSegment(sketch, "E7.5.3.4", {"start": v(-21.13, -36.78) * mm, "end": v(-18.89, -34.54) * mm});
            skLineSegment(sketch, "E7.5.3.5", {"start": v(-18.89, -34.54) * mm, "end": v(-18.89, -31.36) * mm});
            skLineSegment(sketch, "E7.5.3.6", {"start": v(-26.55, -34.54) * mm, "end": v(-24.3, -36.78) * mm});
            skLineSegment(sketch, "E7.5.3.7", {"start": v(-26.55, -34.54) * mm, "end": v(-26.55, -31.36) * mm});
            skLineSegment(sketch, "E7.5.4.0", {"start": v(-24.3, -26.62) * mm, "end": v(-21.13, -26.62) * mm});
            skLineSegment(sketch, "E7.5.4.1", {"start": v(-26.55, -21.2) * mm, "end": v(-24.3, -18.96) * mm});
            skLineSegment(sketch, "E7.5.4.2", {"start": v(-21.13, -18.96) * mm, "end": v(-18.89, -21.2) * mm});
            skLineSegment(sketch, "E7.5.4.3", {"start": v(-24.3, -18.96) * mm, "end": v(-21.13, -18.96) * mm});
            skLineSegment(sketch, "E7.5.4.4", {"start": v(-21.13, -26.62) * mm, "end": v(-18.89, -24.38) * mm});
            skLineSegment(sketch, "E7.5.4.5", {"start": v(-18.89, -24.38) * mm, "end": v(-18.89, -21.2) * mm});
            skLineSegment(sketch, "E7.5.4.6", {"start": v(-26.55, -24.38) * mm, "end": v(-24.3, -26.62) * mm});
            skLineSegment(sketch, "E7.5.4.7", {"start": v(-26.55, -24.38) * mm, "end": v(-26.55, -21.2) * mm});
            skLineSegment(sketch, "E7.5.5.0", {"start": v(-24.3, -16.46) * mm, "end": v(-21.13, -16.46) * mm});
            skLineSegment(sketch, "E7.5.5.1", {"start": v(-26.55, -11.04) * mm, "end": v(-24.3, -8.8) * mm});
            skLineSegment(sketch, "E7.5.5.2", {"start": v(-21.13, -8.8) * mm, "end": v(-18.89, -11.04) * mm});
            skLineSegment(sketch, "E7.5.5.3", {"start": v(-24.3, -8.8) * mm, "end": v(-21.13, -8.8) * mm});
            skLineSegment(sketch, "E7.5.5.4", {"start": v(-21.13, -16.46) * mm, "end": v(-18.89, -14.22) * mm});
            skLineSegment(sketch, "E7.5.5.5", {"start": v(-18.89, -14.22) * mm, "end": v(-18.89, -11.04) * mm});
            skLineSegment(sketch, "E7.5.5.6", {"start": v(-26.55, -14.22) * mm, "end": v(-24.3, -16.46) * mm});
            skLineSegment(sketch, "E7.5.5.7", {"start": v(-26.55, -14.22) * mm, "end": v(-26.55, -11.04) * mm});
            skLineSegment(sketch, "E7.5.6.0", {"start": v(-24.3, -6.3) * mm, "end": v(-21.13, -6.3) * mm});
            skLineSegment(sketch, "E7.5.6.1", {"start": v(-26.55, -0.88) * mm, "end": v(-24.3, 1.36) * mm});
            skLineSegment(sketch, "E7.5.6.2", {"start": v(-21.13, 1.36) * mm, "end": v(-18.89, -0.88) * mm});
            skLineSegment(sketch, "E7.5.6.3", {"start": v(-24.3, 1.36) * mm, "end": v(-21.13, 1.36) * mm});
            skLineSegment(sketch, "E7.5.6.4", {"start": v(-21.13, -6.3) * mm, "end": v(-18.89, -4.06) * mm});
            skLineSegment(sketch, "E7.5.6.5", {"start": v(-18.89, -4.06) * mm, "end": v(-18.89, -0.88) * mm});
            skLineSegment(sketch, "E7.5.6.6", {"start": v(-26.55, -4.06) * mm, "end": v(-24.3, -6.3) * mm});
            skLineSegment(sketch, "E7.5.6.7", {"start": v(-26.55, -4.06) * mm, "end": v(-26.55, -0.88) * mm});
            skLineSegment(sketch, "E7.5.7.0", {"start": v(-24.3, 3.86) * mm, "end": v(-21.13, 3.86) * mm});
            skLineSegment(sketch, "E7.5.7.1", {"start": v(-26.55, 9.28) * mm, "end": v(-24.3, 11.52) * mm});
            skLineSegment(sketch, "E7.5.7.2", {"start": v(-21.13, 11.52) * mm, "end": v(-18.89, 9.28) * mm});
            skLineSegment(sketch, "E7.5.7.3", {"start": v(-24.3, 11.52) * mm, "end": v(-21.13, 11.52) * mm});
            skLineSegment(sketch, "E7.5.7.4", {"start": v(-21.13, 3.86) * mm, "end": v(-18.89, 6.1) * mm});
            skLineSegment(sketch, "E7.5.7.5", {"start": v(-18.89, 6.1) * mm, "end": v(-18.89, 9.28) * mm});
            skLineSegment(sketch, "E7.5.7.6", {"start": v(-26.55, 6.1) * mm, "end": v(-24.3, 3.86) * mm});
            skLineSegment(sketch, "E7.5.7.7", {"start": v(-26.55, 6.1) * mm, "end": v(-26.55, 9.28) * mm});
            skLineSegment(sketch, "E7.5.8.0", {"start": v(-24.3, 14.02) * mm, "end": v(-21.13, 14.02) * mm});
            skLineSegment(sketch, "E7.5.8.1", {"start": v(-26.55, 19.44) * mm, "end": v(-24.3, 21.68) * mm});
            skLineSegment(sketch, "E7.5.8.2", {"start": v(-21.13, 21.68) * mm, "end": v(-18.89, 19.44) * mm});
            skLineSegment(sketch, "E7.5.8.3", {"start": v(-24.3, 21.68) * mm, "end": v(-21.13, 21.68) * mm});
            skLineSegment(sketch, "E7.5.8.4", {"start": v(-21.13, 14.02) * mm, "end": v(-18.89, 16.26) * mm});
            skLineSegment(sketch, "E7.5.8.5", {"start": v(-18.89, 16.26) * mm, "end": v(-18.89, 19.44) * mm});
            skLineSegment(sketch, "E7.5.8.6", {"start": v(-26.55, 16.26) * mm, "end": v(-24.3, 14.02) * mm});
            skLineSegment(sketch, "E7.5.8.7", {"start": v(-26.55, 16.26) * mm, "end": v(-26.55, 19.44) * mm});
            skLineSegment(sketch, "E7.5.9.0", {"start": v(-24.3, 24.18) * mm, "end": v(-21.13, 24.18) * mm});
            skLineSegment(sketch, "E7.5.9.1", {"start": v(-26.55, 29.6) * mm, "end": v(-24.3, 31.84) * mm});
            skLineSegment(sketch, "E7.5.9.2", {"start": v(-21.13, 31.84) * mm, "end": v(-18.89, 29.6) * mm});
            skLineSegment(sketch, "E7.5.9.3", {"start": v(-24.3, 31.84) * mm, "end": v(-21.13, 31.84) * mm});
            skLineSegment(sketch, "E7.5.9.4", {"start": v(-21.13, 24.18) * mm, "end": v(-18.89, 26.42) * mm});
            skLineSegment(sketch, "E7.5.9.5", {"start": v(-18.89, 26.42) * mm, "end": v(-18.89, 29.6) * mm});
            skLineSegment(sketch, "E7.5.9.6", {"start": v(-26.55, 26.42) * mm, "end": v(-24.3, 24.18) * mm});
            skLineSegment(sketch, "E7.5.9.7", {"start": v(-26.55, 26.42) * mm, "end": v(-26.55, 29.6) * mm});
            skLineSegment(sketch, "E7.5.10.0", {"start": v(-24.3, 34.34) * mm, "end": v(-21.13, 34.34) * mm});
            skLineSegment(sketch, "E7.5.10.1", {"start": v(-26.55, 39.76) * mm, "end": v(-24.3, 42) * mm});
            skLineSegment(sketch, "E7.5.10.2", {"start": v(-21.13, 42) * mm, "end": v(-18.89, 39.76) * mm});
            skLineSegment(sketch, "E7.5.10.3", {"start": v(-24.3, 42) * mm, "end": v(-21.13, 42) * mm});
            skLineSegment(sketch, "E7.5.10.4", {"start": v(-21.13, 34.34) * mm, "end": v(-18.89, 36.58) * mm});
            skLineSegment(sketch, "E7.5.10.5", {"start": v(-18.89, 36.58) * mm, "end": v(-18.89, 39.76) * mm});
            skLineSegment(sketch, "E7.5.10.6", {"start": v(-26.55, 36.58) * mm, "end": v(-24.3, 34.34) * mm});
            skLineSegment(sketch, "E7.5.10.7", {"start": v(-26.55, 36.58) * mm, "end": v(-26.55, 39.76) * mm});
            skLineSegment(sketch, "E7.5.11.0", {"start": v(-24.3, 44.5) * mm, "end": v(-21.13, 44.5) * mm});
            skLineSegment(sketch, "E7.5.11.1", {"start": v(-26.55, 49.92) * mm, "end": v(-24.3, 52.16) * mm});
            skLineSegment(sketch, "E7.5.11.2", {"start": v(-21.13, 52.16) * mm, "end": v(-18.89, 49.92) * mm});
            skLineSegment(sketch, "E7.5.11.3", {"start": v(-24.3, 52.16) * mm, "end": v(-21.13, 52.16) * mm});
            skLineSegment(sketch, "E7.5.11.4", {"start": v(-21.13, 44.5) * mm, "end": v(-18.89, 46.74) * mm});
            skLineSegment(sketch, "E7.5.11.5", {"start": v(-18.89, 46.74) * mm, "end": v(-18.89, 49.92) * mm});
            skLineSegment(sketch, "E7.5.11.6", {"start": v(-26.55, 46.74) * mm, "end": v(-24.3, 44.5) * mm});
            skLineSegment(sketch, "E7.5.11.7", {"start": v(-26.55, 46.74) * mm, "end": v(-26.55, 49.92) * mm});
            skLineSegment(sketch, "E7.5.12.0", {"start": v(-24.3, 54.66) * mm, "end": v(-21.13, 54.66) * mm});
            skLineSegment(sketch, "E7.5.12.1", {"start": v(-26.55, 60.08) * mm, "end": v(-24.3, 62.32) * mm});
            skLineSegment(sketch, "E7.5.12.2", {"start": v(-21.13, 62.32) * mm, "end": v(-18.89, 60.08) * mm});
            skLineSegment(sketch, "E7.5.12.3", {"start": v(-24.3, 62.32) * mm, "end": v(-21.13, 62.32) * mm});
            skLineSegment(sketch, "E7.5.12.4", {"start": v(-21.13, 54.66) * mm, "end": v(-18.89, 56.9) * mm});
            skLineSegment(sketch, "E7.5.12.5", {"start": v(-18.89, 56.9) * mm, "end": v(-18.89, 60.08) * mm});
            skLineSegment(sketch, "E7.5.12.6", {"start": v(-26.55, 56.9) * mm, "end": v(-24.3, 54.66) * mm});
            skLineSegment(sketch, "E7.5.12.7", {"start": v(-26.55, 56.9) * mm, "end": v(-26.55, 60.08) * mm});
            skLineSegment(sketch, "E7.5.13.0", {"start": v(-24.3, 64.82) * mm, "end": v(-21.13, 64.82) * mm});
            skLineSegment(sketch, "E7.5.13.4", {"start": v(-21.13, 64.82) * mm, "end": v(-18.89, 67.06) * mm});
            skLineSegment(sketch, "E7.5.13.5", {"start": v(-18.89, 67.06) * mm, "end": v(-18.89, 67.7) * mm});
            skLineSegment(sketch, "E7.5.13.6", {"start": v(-24.78, 65.3) * mm, "end": v(-24.3, 64.82) * mm});
            skLineSegment(sketch, "E7.6.0.1", {"start": v(-17.66, -61.84) * mm, "end": v(-15.42, -59.6) * mm});
            skLineSegment(sketch, "E7.6.0.2", {"start": v(-12.24, -59.6) * mm, "end": v(-10, -61.84) * mm});
            skLineSegment(sketch, "E7.6.0.3", {"start": v(-15.42, -59.6) * mm, "end": v(-12.24, -59.6) * mm});
            skLineSegment(sketch, "E7.6.1.0", {"start": v(-15.42, -57.1) * mm, "end": v(-12.24, -57.1) * mm});
            skLineSegment(sketch, "E7.6.1.1", {"start": v(-17.66, -51.68) * mm, "end": v(-15.42, -49.44) * mm});
            skLineSegment(sketch, "E7.6.1.2", {"start": v(-12.24, -49.44) * mm, "end": v(-10, -51.68) * mm});
            skLineSegment(sketch, "E7.6.1.3", {"start": v(-15.42, -49.44) * mm, "end": v(-12.24, -49.44) * mm});
            skLineSegment(sketch, "E7.6.1.4", {"start": v(-12.24, -57.1) * mm, "end": v(-10, -54.86) * mm});
            skLineSegment(sketch, "E7.6.1.5", {"start": v(-10, -54.86) * mm, "end": v(-10, -51.68) * mm});
            skLineSegment(sketch, "E7.6.1.6", {"start": v(-17.66, -54.86) * mm, "end": v(-15.42, -57.1) * mm});
            skLineSegment(sketch, "E7.6.1.7", {"start": v(-17.66, -54.86) * mm, "end": v(-17.66, -51.68) * mm});
            skLineSegment(sketch, "E7.6.2.0", {"start": v(-15.42, -46.94) * mm, "end": v(-12.24, -46.94) * mm});
            skLineSegment(sketch, "E7.6.2.1", {"start": v(-17.66, -41.52) * mm, "end": v(-15.42, -39.28) * mm});
            skLineSegment(sketch, "E7.6.2.2", {"start": v(-12.24, -39.28) * mm, "end": v(-10, -41.52) * mm});
            skLineSegment(sketch, "E7.6.2.3", {"start": v(-15.42, -39.28) * mm, "end": v(-12.24, -39.28) * mm});
            skLineSegment(sketch, "E7.6.2.4", {"start": v(-12.24, -46.94) * mm, "end": v(-10, -44.7) * mm});
            skLineSegment(sketch, "E7.6.2.5", {"start": v(-10, -44.7) * mm, "end": v(-10, -41.52) * mm});
            skLineSegment(sketch, "E7.6.2.6", {"start": v(-17.66, -44.7) * mm, "end": v(-15.42, -46.94) * mm});
            skLineSegment(sketch, "E7.6.2.7", {"start": v(-17.66, -44.7) * mm, "end": v(-17.66, -41.52) * mm});
            skLineSegment(sketch, "E7.6.3.0", {"start": v(-15.42, -36.78) * mm, "end": v(-12.24, -36.78) * mm});
            skLineSegment(sketch, "E7.6.3.1", {"start": v(-17.66, -31.36) * mm, "end": v(-15.42, -29.12) * mm});
            skLineSegment(sketch, "E7.6.3.2", {"start": v(-12.24, -29.12) * mm, "end": v(-10, -31.36) * mm});
            skLineSegment(sketch, "E7.6.3.3", {"start": v(-15.42, -29.12) * mm, "end": v(-12.24, -29.12) * mm});
            skLineSegment(sketch, "E7.6.3.4", {"start": v(-12.24, -36.78) * mm, "end": v(-10, -34.54) * mm});
            skLineSegment(sketch, "E7.6.3.5", {"start": v(-10, -34.54) * mm, "end": v(-10, -31.36) * mm});
            skLineSegment(sketch, "E7.6.3.6", {"start": v(-17.66, -34.54) * mm, "end": v(-15.42, -36.78) * mm});
            skLineSegment(sketch, "E7.6.3.7", {"start": v(-17.66, -34.54) * mm, "end": v(-17.66, -31.36) * mm});
            skLineSegment(sketch, "E7.6.4.0", {"start": v(-15.42, -26.62) * mm, "end": v(-12.24, -26.62) * mm});
            skLineSegment(sketch, "E7.6.4.1", {"start": v(-17.66, -21.2) * mm, "end": v(-15.42, -18.96) * mm});
            skLineSegment(sketch, "E7.6.4.2", {"start": v(-12.24, -18.96) * mm, "end": v(-10, -21.2) * mm});
            skLineSegment(sketch, "E7.6.4.3", {"start": v(-15.42, -18.96) * mm, "end": v(-12.24, -18.96) * mm});
            skLineSegment(sketch, "E7.6.4.4", {"start": v(-12.24, -26.62) * mm, "end": v(-10, -24.38) * mm});
            skLineSegment(sketch, "E7.6.4.5", {"start": v(-10, -24.38) * mm, "end": v(-10, -21.2) * mm});
            skLineSegment(sketch, "E7.6.4.6", {"start": v(-17.66, -24.38) * mm, "end": v(-15.42, -26.62) * mm});
            skLineSegment(sketch, "E7.6.4.7", {"start": v(-17.66, -24.38) * mm, "end": v(-17.66, -21.2) * mm});
            skLineSegment(sketch, "E7.6.5.0", {"start": v(-15.42, -16.46) * mm, "end": v(-12.24, -16.46) * mm});
            skLineSegment(sketch, "E7.6.5.1", {"start": v(-17.66, -11.04) * mm, "end": v(-15.42, -8.8) * mm});
            skLineSegment(sketch, "E7.6.5.2", {"start": v(-12.24, -8.8) * mm, "end": v(-10, -11.04) * mm});
            skLineSegment(sketch, "E7.6.5.3", {"start": v(-15.42, -8.8) * mm, "end": v(-12.24, -8.8) * mm});
            skLineSegment(sketch, "E7.6.5.4", {"start": v(-12.24, -16.46) * mm, "end": v(-10, -14.22) * mm});
            skLineSegment(sketch, "E7.6.5.5", {"start": v(-10, -14.22) * mm, "end": v(-10, -11.04) * mm});
            skLineSegment(sketch, "E7.6.5.6", {"start": v(-17.66, -14.22) * mm, "end": v(-15.42, -16.46) * mm});
            skLineSegment(sketch, "E7.6.5.7", {"start": v(-17.66, -14.22) * mm, "end": v(-17.66, -11.04) * mm});
            skLineSegment(sketch, "E7.6.6.0", {"start": v(-15.42, -6.3) * mm, "end": v(-12.24, -6.3) * mm});
            skLineSegment(sketch, "E7.6.6.1", {"start": v(-17.66, -0.88) * mm, "end": v(-15.42, 1.36) * mm});
            skLineSegment(sketch, "E7.6.6.2", {"start": v(-12.24, 1.36) * mm, "end": v(-10, -0.88) * mm});
            skLineSegment(sketch, "E7.6.6.3", {"start": v(-15.42, 1.36) * mm, "end": v(-12.24, 1.36) * mm});
            skLineSegment(sketch, "E7.6.6.4", {"start": v(-12.24, -6.3) * mm, "end": v(-10, -4.06) * mm});
            skLineSegment(sketch, "E7.6.6.5", {"start": v(-10, -4.06) * mm, "end": v(-10, -0.88) * mm});
            skLineSegment(sketch, "E7.6.6.6", {"start": v(-17.66, -4.06) * mm, "end": v(-15.42, -6.3) * mm});
            skLineSegment(sketch, "E7.6.6.7", {"start": v(-17.66, -4.06) * mm, "end": v(-17.66, -0.88) * mm});
            skLineSegment(sketch, "E7.6.7.0", {"start": v(-15.42, 3.86) * mm, "end": v(-12.24, 3.86) * mm});
            skLineSegment(sketch, "E7.6.7.1", {"start": v(-17.66, 9.28) * mm, "end": v(-15.42, 11.52) * mm});
            skLineSegment(sketch, "E7.6.7.2", {"start": v(-12.24, 11.52) * mm, "end": v(-10, 9.28) * mm});
            skLineSegment(sketch, "E7.6.7.3", {"start": v(-15.42, 11.52) * mm, "end": v(-12.24, 11.52) * mm});
            skLineSegment(sketch, "E7.6.7.4", {"start": v(-12.24, 3.86) * mm, "end": v(-10, 6.1) * mm});
            skLineSegment(sketch, "E7.6.7.5", {"start": v(-10, 6.1) * mm, "end": v(-10, 9.28) * mm});
            skLineSegment(sketch, "E7.6.7.6", {"start": v(-17.66, 6.1) * mm, "end": v(-15.42, 3.86) * mm});
            skLineSegment(sketch, "E7.6.7.7", {"start": v(-17.66, 6.1) * mm, "end": v(-17.66, 9.28) * mm});
            skLineSegment(sketch, "E7.6.8.0", {"start": v(-15.42, 14.02) * mm, "end": v(-12.24, 14.02) * mm});
            skLineSegment(sketch, "E7.6.8.1", {"start": v(-17.66, 19.44) * mm, "end": v(-15.42, 21.68) * mm});
            skLineSegment(sketch, "E7.6.8.2", {"start": v(-12.24, 21.68) * mm, "end": v(-10, 19.44) * mm});
            skLineSegment(sketch, "E7.6.8.3", {"start": v(-15.42, 21.68) * mm, "end": v(-12.24, 21.68) * mm});
            skLineSegment(sketch, "E7.6.8.4", {"start": v(-12.24, 14.02) * mm, "end": v(-10, 16.26) * mm});
            skLineSegment(sketch, "E7.6.8.5", {"start": v(-10, 16.26) * mm, "end": v(-10, 19.44) * mm});
            skLineSegment(sketch, "E7.6.8.6", {"start": v(-17.66, 16.26) * mm, "end": v(-15.42, 14.02) * mm});
            skLineSegment(sketch, "E7.6.8.7", {"start": v(-17.66, 16.26) * mm, "end": v(-17.66, 19.44) * mm});
            skLineSegment(sketch, "E7.6.9.0", {"start": v(-15.42, 24.18) * mm, "end": v(-12.24, 24.18) * mm});
            skLineSegment(sketch, "E7.6.9.1", {"start": v(-17.66, 29.6) * mm, "end": v(-15.42, 31.84) * mm});
            skLineSegment(sketch, "E7.6.9.2", {"start": v(-12.24, 31.84) * mm, "end": v(-10, 29.6) * mm});
            skLineSegment(sketch, "E7.6.9.3", {"start": v(-15.42, 31.84) * mm, "end": v(-12.24, 31.84) * mm});
            skLineSegment(sketch, "E7.6.9.4", {"start": v(-12.24, 24.18) * mm, "end": v(-10, 26.42) * mm});
            skLineSegment(sketch, "E7.6.9.5", {"start": v(-10, 26.42) * mm, "end": v(-10, 29.6) * mm});
            skLineSegment(sketch, "E7.6.9.6", {"start": v(-17.66, 26.42) * mm, "end": v(-15.42, 24.18) * mm});
            skLineSegment(sketch, "E7.6.9.7", {"start": v(-17.66, 26.42) * mm, "end": v(-17.66, 29.6) * mm});
            skLineSegment(sketch, "E7.6.10.0", {"start": v(-15.42, 34.34) * mm, "end": v(-12.24, 34.34) * mm});
            skLineSegment(sketch, "E7.6.10.1", {"start": v(-17.66, 39.76) * mm, "end": v(-15.42, 42) * mm});
            skLineSegment(sketch, "E7.6.10.2", {"start": v(-12.24, 42) * mm, "end": v(-10, 39.76) * mm});
            skLineSegment(sketch, "E7.6.10.3", {"start": v(-15.42, 42) * mm, "end": v(-12.24, 42) * mm});
            skLineSegment(sketch, "E7.6.10.4", {"start": v(-12.24, 34.34) * mm, "end": v(-10, 36.58) * mm});
            skLineSegment(sketch, "E7.6.10.5", {"start": v(-10, 36.58) * mm, "end": v(-10, 39.76) * mm});
            skLineSegment(sketch, "E7.6.10.6", {"start": v(-17.66, 36.58) * mm, "end": v(-15.42, 34.34) * mm});
            skLineSegment(sketch, "E7.6.10.7", {"start": v(-17.66, 36.58) * mm, "end": v(-17.66, 39.76) * mm});
            skLineSegment(sketch, "E7.6.11.0", {"start": v(-15.42, 44.5) * mm, "end": v(-12.24, 44.5) * mm});
            skLineSegment(sketch, "E7.6.11.1", {"start": v(-17.66, 49.92) * mm, "end": v(-15.42, 52.16) * mm});
            skLineSegment(sketch, "E7.6.11.2", {"start": v(-12.24, 52.16) * mm, "end": v(-10, 49.92) * mm});
            skLineSegment(sketch, "E7.6.11.3", {"start": v(-15.42, 52.16) * mm, "end": v(-12.24, 52.16) * mm});
            skLineSegment(sketch, "E7.6.11.4", {"start": v(-12.24, 44.5) * mm, "end": v(-10, 46.74) * mm});
            skLineSegment(sketch, "E7.6.11.5", {"start": v(-10, 46.74) * mm, "end": v(-10, 49.92) * mm});
            skLineSegment(sketch, "E7.6.11.6", {"start": v(-17.66, 46.74) * mm, "end": v(-15.42, 44.5) * mm});
            skLineSegment(sketch, "E7.6.11.7", {"start": v(-17.66, 46.74) * mm, "end": v(-17.66, 49.92) * mm});
            skLineSegment(sketch, "E7.6.12.0", {"start": v(-15.42, 54.66) * mm, "end": v(-12.24, 54.66) * mm});
            skLineSegment(sketch, "E7.6.12.1", {"start": v(-17.66, 60.08) * mm, "end": v(-15.42, 62.32) * mm});
            skLineSegment(sketch, "E7.6.12.2", {"start": v(-12.24, 62.32) * mm, "end": v(-10, 60.08) * mm});
            skLineSegment(sketch, "E7.6.12.3", {"start": v(-15.42, 62.32) * mm, "end": v(-12.24, 62.32) * mm});
            skLineSegment(sketch, "E7.6.12.4", {"start": v(-12.24, 54.66) * mm, "end": v(-10, 56.9) * mm});
            skLineSegment(sketch, "E7.6.12.5", {"start": v(-10, 56.9) * mm, "end": v(-10, 60.08) * mm});
            skLineSegment(sketch, "E7.6.12.6", {"start": v(-17.66, 56.9) * mm, "end": v(-15.42, 54.66) * mm});
            skLineSegment(sketch, "E7.6.12.7", {"start": v(-17.66, 56.9) * mm, "end": v(-17.66, 60.08) * mm});
            skLineSegment(sketch, "E7.6.13.0", {"start": v(-15.42, 64.82) * mm, "end": v(-12.24, 64.82) * mm});
            skLineSegment(sketch, "E7.6.13.4", {"start": v(-12.24, 64.82) * mm, "end": v(-10, 67.06) * mm});
            skLineSegment(sketch, "E7.6.13.5", {"start": v(-10, 67.06) * mm, "end": v(-10, 69.98) * mm});
            skLineSegment(sketch, "E7.6.13.6", {"start": v(-17.66, 67.06) * mm, "end": v(-15.42, 64.82) * mm});
            skLineSegment(sketch, "E7.6.13.7", {"start": v(-17.66, 67.06) * mm, "end": v(-17.66, 68.1) * mm});
            skLineSegment(sketch, "E7.7.0.1", {"start": v(-8.77, -61.84) * mm, "end": v(-6.53, -59.6) * mm});
            skLineSegment(sketch, "E7.7.0.2", {"start": v(-3.35, -59.6) * mm, "end": v(-1.1, -61.84) * mm});
            skLineSegment(sketch, "E7.7.0.3", {"start": v(-6.53, -59.6) * mm, "end": v(-3.35, -59.6) * mm});
            skLineSegment(sketch, "E7.7.1.0", {"start": v(-6.53, -57.1) * mm, "end": v(-3.35, -57.1) * mm});
            skLineSegment(sketch, "E7.7.1.1", {"start": v(-8.77, -51.68) * mm, "end": v(-6.53, -49.44) * mm});
            skLineSegment(sketch, "E7.7.1.2", {"start": v(-3.35, -49.44) * mm, "end": v(-1.1, -51.68) * mm});
            skLineSegment(sketch, "E7.7.1.3", {"start": v(-6.53, -49.44) * mm, "end": v(-3.35, -49.44) * mm});
            skLineSegment(sketch, "E7.7.1.4", {"start": v(-3.35, -57.1) * mm, "end": v(-1.1, -54.86) * mm});
            skLineSegment(sketch, "E7.7.1.5", {"start": v(-1.1, -54.86) * mm, "end": v(-1.1, -51.68) * mm});
            skLineSegment(sketch, "E7.7.1.6", {"start": v(-8.77, -54.86) * mm, "end": v(-6.53, -57.1) * mm});
            skLineSegment(sketch, "E7.7.1.7", {"start": v(-8.77, -54.86) * mm, "end": v(-8.77, -51.68) * mm});
            skLineSegment(sketch, "E7.7.2.0", {"start": v(-6.53, -46.94) * mm, "end": v(-3.35, -46.94) * mm});
            skLineSegment(sketch, "E7.7.2.1", {"start": v(-8.77, -41.52) * mm, "end": v(-6.53, -39.28) * mm});
            skLineSegment(sketch, "E7.7.2.2", {"start": v(-3.35, -39.28) * mm, "end": v(-1.1, -41.52) * mm});
            skLineSegment(sketch, "E7.7.2.3", {"start": v(-6.53, -39.28) * mm, "end": v(-3.35, -39.28) * mm});
            skLineSegment(sketch, "E7.7.2.4", {"start": v(-3.35, -46.94) * mm, "end": v(-1.1, -44.7) * mm});
            skLineSegment(sketch, "E7.7.2.5", {"start": v(-1.1, -44.7) * mm, "end": v(-1.1, -41.52) * mm});
            skLineSegment(sketch, "E7.7.2.6", {"start": v(-8.77, -44.7) * mm, "end": v(-6.53, -46.94) * mm});
            skLineSegment(sketch, "E7.7.2.7", {"start": v(-8.77, -44.7) * mm, "end": v(-8.77, -41.52) * mm});
            skLineSegment(sketch, "E7.7.3.0", {"start": v(-6.53, -36.78) * mm, "end": v(-3.35, -36.78) * mm});
            skLineSegment(sketch, "E7.7.3.1", {"start": v(-8.77, -31.36) * mm, "end": v(-6.53, -29.12) * mm});
            skLineSegment(sketch, "E7.7.3.2", {"start": v(-3.35, -29.12) * mm, "end": v(-1.1, -31.36) * mm});
            skLineSegment(sketch, "E7.7.3.3", {"start": v(-6.53, -29.12) * mm, "end": v(-3.35, -29.12) * mm});
            skLineSegment(sketch, "E7.7.3.4", {"start": v(-3.35, -36.78) * mm, "end": v(-1.1, -34.54) * mm});
            skLineSegment(sketch, "E7.7.3.5", {"start": v(-1.1, -34.54) * mm, "end": v(-1.1, -31.36) * mm});
            skLineSegment(sketch, "E7.7.3.6", {"start": v(-8.77, -34.54) * mm, "end": v(-6.53, -36.78) * mm});
            skLineSegment(sketch, "E7.7.3.7", {"start": v(-8.77, -34.54) * mm, "end": v(-8.77, -31.36) * mm});
            skLineSegment(sketch, "E7.7.4.0", {"start": v(-6.53, -26.62) * mm, "end": v(-3.35, -26.62) * mm});
            skLineSegment(sketch, "E7.7.4.1", {"start": v(-8.77, -21.2) * mm, "end": v(-6.53, -18.96) * mm});
            skLineSegment(sketch, "E7.7.4.2", {"start": v(-3.35, -18.96) * mm, "end": v(-1.1, -21.2) * mm});
            skLineSegment(sketch, "E7.7.4.3", {"start": v(-6.53, -18.96) * mm, "end": v(-3.35, -18.96) * mm});
            skLineSegment(sketch, "E7.7.4.4", {"start": v(-3.35, -26.62) * mm, "end": v(-1.1, -24.38) * mm});
            skLineSegment(sketch, "E7.7.4.5", {"start": v(-1.1, -24.38) * mm, "end": v(-1.1, -21.2) * mm});
            skLineSegment(sketch, "E7.7.4.6", {"start": v(-8.77, -24.38) * mm, "end": v(-6.53, -26.62) * mm});
            skLineSegment(sketch, "E7.7.4.7", {"start": v(-8.77, -24.38) * mm, "end": v(-8.77, -21.2) * mm});
            skLineSegment(sketch, "E7.7.5.0", {"start": v(-6.53, -16.46) * mm, "end": v(-3.35, -16.46) * mm});
            skLineSegment(sketch, "E7.7.5.1", {"start": v(-8.77, -11.04) * mm, "end": v(-6.53, -8.8) * mm});
            skLineSegment(sketch, "E7.7.5.2", {"start": v(-3.35, -8.8) * mm, "end": v(-1.1, -11.04) * mm});
            skLineSegment(sketch, "E7.7.5.3", {"start": v(-6.53, -8.8) * mm, "end": v(-3.35, -8.8) * mm});
            skLineSegment(sketch, "E7.7.5.4", {"start": v(-3.35, -16.46) * mm, "end": v(-1.1, -14.22) * mm});
            skLineSegment(sketch, "E7.7.5.5", {"start": v(-1.1, -14.22) * mm, "end": v(-1.1, -11.04) * mm});
            skLineSegment(sketch, "E7.7.5.6", {"start": v(-8.77, -14.22) * mm, "end": v(-6.53, -16.46) * mm});
            skLineSegment(sketch, "E7.7.5.7", {"start": v(-8.77, -14.22) * mm, "end": v(-8.77, -11.04) * mm});
            skLineSegment(sketch, "E7.7.6.0", {"start": v(-6.53, -6.3) * mm, "end": v(-3.35, -6.3) * mm});
            skLineSegment(sketch, "E7.7.6.1", {"start": v(-8.77, -0.88) * mm, "end": v(-6.53, 1.36) * mm});
            skLineSegment(sketch, "E7.7.6.2", {"start": v(-3.35, 1.36) * mm, "end": v(-1.1, -0.88) * mm});
            skLineSegment(sketch, "E7.7.6.3", {"start": v(-6.53, 1.36) * mm, "end": v(-3.35, 1.36) * mm});
            skLineSegment(sketch, "E7.7.6.4", {"start": v(-3.35, -6.3) * mm, "end": v(-1.1, -4.06) * mm});
            skLineSegment(sketch, "E7.7.6.5", {"start": v(-1.1, -4.06) * mm, "end": v(-1.1, -0.88) * mm});
            skLineSegment(sketch, "E7.7.6.6", {"start": v(-8.77, -4.06) * mm, "end": v(-6.53, -6.3) * mm});
            skLineSegment(sketch, "E7.7.6.7", {"start": v(-8.77, -4.06) * mm, "end": v(-8.77, -0.88) * mm});
            skLineSegment(sketch, "E7.7.7.0", {"start": v(-6.53, 3.86) * mm, "end": v(-3.35, 3.86) * mm});
            skLineSegment(sketch, "E7.7.7.1", {"start": v(-8.77, 9.28) * mm, "end": v(-6.53, 11.52) * mm});
            skLineSegment(sketch, "E7.7.7.2", {"start": v(-3.35, 11.52) * mm, "end": v(-1.1, 9.28) * mm});
            skLineSegment(sketch, "E7.7.7.3", {"start": v(-6.53, 11.52) * mm, "end": v(-3.35, 11.52) * mm});
            skLineSegment(sketch, "E7.7.7.4", {"start": v(-3.35, 3.86) * mm, "end": v(-1.1, 6.1) * mm});
            skLineSegment(sketch, "E7.7.7.5", {"start": v(-1.1, 6.1) * mm, "end": v(-1.1, 9.28) * mm});
            skLineSegment(sketch, "E7.7.7.6", {"start": v(-8.77, 6.1) * mm, "end": v(-6.53, 3.86) * mm});
            skLineSegment(sketch, "E7.7.7.7", {"start": v(-8.77, 6.1) * mm, "end": v(-8.77, 9.28) * mm});
            skLineSegment(sketch, "E7.7.8.0", {"start": v(-6.53, 14.02) * mm, "end": v(-3.35, 14.02) * mm});
            skLineSegment(sketch, "E7.7.8.1", {"start": v(-8.77, 19.44) * mm, "end": v(-6.53, 21.68) * mm});
            skLineSegment(sketch, "E7.7.8.2", {"start": v(-3.35, 21.68) * mm, "end": v(-1.1, 19.44) * mm});
            skLineSegment(sketch, "E7.7.8.3", {"start": v(-6.53, 21.68) * mm, "end": v(-3.35, 21.68) * mm});
            skLineSegment(sketch, "E7.7.8.4", {"start": v(-3.35, 14.02) * mm, "end": v(-1.1, 16.26) * mm});
            skLineSegment(sketch, "E7.7.8.5", {"start": v(-1.1, 16.26) * mm, "end": v(-1.1, 19.44) * mm});
            skLineSegment(sketch, "E7.7.8.6", {"start": v(-8.77, 16.26) * mm, "end": v(-6.53, 14.02) * mm});
            skLineSegment(sketch, "E7.7.8.7", {"start": v(-8.77, 16.26) * mm, "end": v(-8.77, 19.44) * mm});
            skLineSegment(sketch, "E7.7.9.0", {"start": v(-6.53, 24.18) * mm, "end": v(-3.35, 24.18) * mm});
            skLineSegment(sketch, "E7.7.9.1", {"start": v(-8.77, 29.6) * mm, "end": v(-6.53, 31.84) * mm});
            skLineSegment(sketch, "E7.7.9.2", {"start": v(-3.35, 31.84) * mm, "end": v(-1.1, 29.6) * mm});
            skLineSegment(sketch, "E7.7.9.3", {"start": v(-6.53, 31.84) * mm, "end": v(-3.35, 31.84) * mm});
            skLineSegment(sketch, "E7.7.9.4", {"start": v(-3.35, 24.18) * mm, "end": v(-1.1, 26.42) * mm});
            skLineSegment(sketch, "E7.7.9.5", {"start": v(-1.1, 26.42) * mm, "end": v(-1.1, 29.6) * mm});
            skLineSegment(sketch, "E7.7.9.6", {"start": v(-8.77, 26.42) * mm, "end": v(-6.53, 24.18) * mm});
            skLineSegment(sketch, "E7.7.9.7", {"start": v(-8.77, 26.42) * mm, "end": v(-8.77, 29.6) * mm});
            skLineSegment(sketch, "E7.7.10.0", {"start": v(-6.53, 34.34) * mm, "end": v(-3.35, 34.34) * mm});
            skLineSegment(sketch, "E7.7.10.1", {"start": v(-8.77, 39.76) * mm, "end": v(-6.53, 42) * mm});
            skLineSegment(sketch, "E7.7.10.2", {"start": v(-3.35, 42) * mm, "end": v(-1.1, 39.76) * mm});
            skLineSegment(sketch, "E7.7.10.3", {"start": v(-6.53, 42) * mm, "end": v(-3.35, 42) * mm});
            skLineSegment(sketch, "E7.7.10.4", {"start": v(-3.35, 34.34) * mm, "end": v(-1.1, 36.58) * mm});
            skLineSegment(sketch, "E7.7.10.5", {"start": v(-1.1, 36.58) * mm, "end": v(-1.1, 39.76) * mm});
            skLineSegment(sketch, "E7.7.10.6", {"start": v(-8.77, 36.58) * mm, "end": v(-6.53, 34.34) * mm});
            skLineSegment(sketch, "E7.7.10.7", {"start": v(-8.77, 36.58) * mm, "end": v(-8.77, 39.76) * mm});
            skLineSegment(sketch, "E7.7.11.0", {"start": v(-6.53, 44.5) * mm, "end": v(-3.35, 44.5) * mm});
            skLineSegment(sketch, "E7.7.11.1", {"start": v(-8.77, 49.92) * mm, "end": v(-6.53, 52.16) * mm});
            skLineSegment(sketch, "E7.7.11.2", {"start": v(-3.35, 52.16) * mm, "end": v(-1.1, 49.92) * mm});
            skLineSegment(sketch, "E7.7.11.3", {"start": v(-6.53, 52.16) * mm, "end": v(-3.35, 52.16) * mm});
            skLineSegment(sketch, "E7.7.11.4", {"start": v(-3.35, 44.5) * mm, "end": v(-1.1, 46.74) * mm});
            skLineSegment(sketch, "E7.7.11.5", {"start": v(-1.1, 46.74) * mm, "end": v(-1.1, 49.92) * mm});
            skLineSegment(sketch, "E7.7.11.6", {"start": v(-8.77, 46.74) * mm, "end": v(-6.53, 44.5) * mm});
            skLineSegment(sketch, "E7.7.11.7", {"start": v(-8.77, 46.74) * mm, "end": v(-8.77, 49.92) * mm});
            skLineSegment(sketch, "E7.7.12.0", {"start": v(-6.53, 54.66) * mm, "end": v(-3.35, 54.66) * mm});
            skLineSegment(sketch, "E7.7.12.1", {"start": v(-8.77, 60.08) * mm, "end": v(-6.53, 62.32) * mm});
            skLineSegment(sketch, "E7.7.12.2", {"start": v(-3.35, 62.32) * mm, "end": v(-1.1, 60.08) * mm});
            skLineSegment(sketch, "E7.7.12.3", {"start": v(-6.53, 62.32) * mm, "end": v(-3.35, 62.32) * mm});
            skLineSegment(sketch, "E7.7.12.4", {"start": v(-3.35, 54.66) * mm, "end": v(-1.1, 56.9) * mm});
            skLineSegment(sketch, "E7.7.12.5", {"start": v(-1.1, 56.9) * mm, "end": v(-1.1, 60.08) * mm});
            skLineSegment(sketch, "E7.7.12.6", {"start": v(-8.77, 56.9) * mm, "end": v(-6.53, 54.66) * mm});
            skLineSegment(sketch, "E7.7.12.7", {"start": v(-8.77, 56.9) * mm, "end": v(-8.77, 60.08) * mm});
            skLineSegment(sketch, "E7.7.13.0", {"start": v(-6.53, 64.82) * mm, "end": v(-3.35, 64.82) * mm});
            skLineSegment(sketch, "E7.7.13.2", {"start": v(-1.7, 70.83) * mm, "end": v(-1.1, 70.24) * mm});
            skLineSegment(sketch, "E7.7.13.4", {"start": v(-3.35, 64.82) * mm, "end": v(-1.1, 67.06) * mm});
            skLineSegment(sketch, "E7.7.13.5", {"start": v(-1.1, 67.06) * mm, "end": v(-1.1, 70.24) * mm});
            skLineSegment(sketch, "E7.7.13.6", {"start": v(-8.77, 67.06) * mm, "end": v(-6.53, 64.82) * mm});
            skLineSegment(sketch, "E7.8.0.1", {"start": v(0.12, -61.84) * mm, "end": v(2.36, -59.6) * mm});
            skLineSegment(sketch, "E7.8.0.2", {"start": v(5.54, -59.6) * mm, "end": v(7.78, -61.84) * mm});
            skLineSegment(sketch, "E7.8.0.3", {"start": v(2.36, -59.6) * mm, "end": v(5.54, -59.6) * mm});
            skLineSegment(sketch, "E7.8.1.0", {"start": v(2.36, -57.1) * mm, "end": v(5.54, -57.1) * mm});
            skLineSegment(sketch, "E7.8.1.1", {"start": v(0.12, -51.68) * mm, "end": v(2.36, -49.44) * mm});
            skLineSegment(sketch, "E7.8.1.2", {"start": v(5.54, -49.44) * mm, "end": v(7.78, -51.68) * mm});
            skLineSegment(sketch, "E7.8.1.3", {"start": v(2.36, -49.44) * mm, "end": v(5.54, -49.44) * mm});
            skLineSegment(sketch, "E7.8.1.4", {"start": v(5.54, -57.1) * mm, "end": v(7.78, -54.86) * mm});
            skLineSegment(sketch, "E7.8.1.5", {"start": v(7.78, -54.86) * mm, "end": v(7.78, -51.68) * mm});
            skLineSegment(sketch, "E7.8.1.6", {"start": v(0.12, -54.86) * mm, "end": v(2.36, -57.1) * mm});
            skLineSegment(sketch, "E7.8.1.7", {"start": v(0.12, -54.86) * mm, "end": v(0.12, -51.68) * mm});
            skLineSegment(sketch, "E7.8.2.0", {"start": v(2.36, -46.94) * mm, "end": v(5.54, -46.94) * mm});
            skLineSegment(sketch, "E7.8.2.1", {"start": v(0.12, -41.52) * mm, "end": v(2.36, -39.28) * mm});
            skLineSegment(sketch, "E7.8.2.2", {"start": v(5.54, -39.28) * mm, "end": v(7.78, -41.52) * mm});
            skLineSegment(sketch, "E7.8.2.3", {"start": v(2.36, -39.28) * mm, "end": v(5.54, -39.28) * mm});
            skLineSegment(sketch, "E7.8.2.4", {"start": v(5.54, -46.94) * mm, "end": v(7.78, -44.7) * mm});
            skLineSegment(sketch, "E7.8.2.5", {"start": v(7.78, -44.7) * mm, "end": v(7.78, -41.52) * mm});
            skLineSegment(sketch, "E7.8.2.6", {"start": v(0.12, -44.7) * mm, "end": v(2.36, -46.94) * mm});
            skLineSegment(sketch, "E7.8.2.7", {"start": v(0.12, -44.7) * mm, "end": v(0.12, -41.52) * mm});
            skLineSegment(sketch, "E7.8.3.0", {"start": v(2.36, -36.78) * mm, "end": v(5.54, -36.78) * mm});
            skLineSegment(sketch, "E7.8.3.1", {"start": v(0.12, -31.36) * mm, "end": v(2.36, -29.12) * mm});
            skLineSegment(sketch, "E7.8.3.2", {"start": v(5.54, -29.12) * mm, "end": v(7.78, -31.36) * mm});
            skLineSegment(sketch, "E7.8.3.3", {"start": v(2.36, -29.12) * mm, "end": v(5.54, -29.12) * mm});
            skLineSegment(sketch, "E7.8.3.4", {"start": v(5.54, -36.78) * mm, "end": v(7.78, -34.54) * mm});
            skLineSegment(sketch, "E7.8.3.5", {"start": v(7.78, -34.54) * mm, "end": v(7.78, -31.36) * mm});
            skLineSegment(sketch, "E7.8.3.6", {"start": v(0.12, -34.54) * mm, "end": v(2.36, -36.78) * mm});
            skLineSegment(sketch, "E7.8.3.7", {"start": v(0.12, -34.54) * mm, "end": v(0.12, -31.36) * mm});
            skLineSegment(sketch, "E7.8.4.0", {"start": v(2.36, -26.62) * mm, "end": v(5.54, -26.62) * mm});
            skLineSegment(sketch, "E7.8.4.1", {"start": v(0.12, -21.2) * mm, "end": v(2.36, -18.96) * mm});
            skLineSegment(sketch, "E7.8.4.2", {"start": v(5.54, -18.96) * mm, "end": v(7.78, -21.2) * mm});
            skLineSegment(sketch, "E7.8.4.3", {"start": v(2.36, -18.96) * mm, "end": v(5.54, -18.96) * mm});
            skLineSegment(sketch, "E7.8.4.4", {"start": v(5.54, -26.62) * mm, "end": v(7.78, -24.38) * mm});
            skLineSegment(sketch, "E7.8.4.5", {"start": v(7.78, -24.38) * mm, "end": v(7.78, -21.2) * mm});
            skLineSegment(sketch, "E7.8.4.6", {"start": v(0.12, -24.38) * mm, "end": v(2.36, -26.62) * mm});
            skLineSegment(sketch, "E7.8.4.7", {"start": v(0.12, -24.38) * mm, "end": v(0.12, -21.2) * mm});
            skLineSegment(sketch, "E7.8.5.0", {"start": v(2.36, -16.46) * mm, "end": v(5.54, -16.46) * mm});
            skLineSegment(sketch, "E7.8.5.1", {"start": v(0.12, -11.04) * mm, "end": v(2.36, -8.8) * mm});
            skLineSegment(sketch, "E7.8.5.2", {"start": v(5.54, -8.8) * mm, "end": v(7.78, -11.04) * mm});
            skLineSegment(sketch, "E7.8.5.3", {"start": v(2.36, -8.8) * mm, "end": v(5.54, -8.8) * mm});
            skLineSegment(sketch, "E7.8.5.4", {"start": v(5.54, -16.46) * mm, "end": v(7.78, -14.22) * mm});
            skLineSegment(sketch, "E7.8.5.5", {"start": v(7.78, -14.22) * mm, "end": v(7.78, -11.04) * mm});
            skLineSegment(sketch, "E7.8.5.6", {"start": v(0.12, -14.22) * mm, "end": v(2.36, -16.46) * mm});
            skLineSegment(sketch, "E7.8.5.7", {"start": v(0.12, -14.22) * mm, "end": v(0.12, -11.04) * mm});
            skLineSegment(sketch, "E7.8.6.0", {"start": v(2.36, -6.3) * mm, "end": v(5.54, -6.3) * mm});
            skLineSegment(sketch, "E7.8.6.1", {"start": v(0.12, -0.88) * mm, "end": v(2.36, 1.36) * mm});
            skLineSegment(sketch, "E7.8.6.2", {"start": v(5.54, 1.36) * mm, "end": v(7.78, -0.88) * mm});
            skLineSegment(sketch, "E7.8.6.3", {"start": v(2.36, 1.36) * mm, "end": v(5.54, 1.36) * mm});
            skLineSegment(sketch, "E7.8.6.4", {"start": v(5.54, -6.3) * mm, "end": v(7.78, -4.06) * mm});
            skLineSegment(sketch, "E7.8.6.5", {"start": v(7.78, -4.06) * mm, "end": v(7.78, -0.88) * mm});
            skLineSegment(sketch, "E7.8.6.6", {"start": v(0.12, -4.06) * mm, "end": v(2.36, -6.3) * mm});
            skLineSegment(sketch, "E7.8.6.7", {"start": v(0.12, -4.06) * mm, "end": v(0.12, -0.88) * mm});
            skLineSegment(sketch, "E7.8.7.0", {"start": v(2.36, 3.86) * mm, "end": v(5.54, 3.86) * mm});
            skLineSegment(sketch, "E7.8.7.1", {"start": v(0.12, 9.28) * mm, "end": v(2.36, 11.52) * mm});
            skLineSegment(sketch, "E7.8.7.2", {"start": v(5.54, 11.52) * mm, "end": v(7.78, 9.28) * mm});
            skLineSegment(sketch, "E7.8.7.3", {"start": v(2.36, 11.52) * mm, "end": v(5.54, 11.52) * mm});
            skLineSegment(sketch, "E7.8.7.4", {"start": v(5.54, 3.86) * mm, "end": v(7.78, 6.1) * mm});
            skLineSegment(sketch, "E7.8.7.5", {"start": v(7.78, 6.1) * mm, "end": v(7.78, 9.28) * mm});
            skLineSegment(sketch, "E7.8.7.6", {"start": v(0.12, 6.1) * mm, "end": v(2.36, 3.86) * mm});
            skLineSegment(sketch, "E7.8.7.7", {"start": v(0.12, 6.1) * mm, "end": v(0.12, 9.28) * mm});
            skLineSegment(sketch, "E7.8.8.0", {"start": v(2.36, 14.02) * mm, "end": v(5.54, 14.02) * mm});
            skLineSegment(sketch, "E7.8.8.1", {"start": v(0.12, 19.44) * mm, "end": v(2.36, 21.68) * mm});
            skLineSegment(sketch, "E7.8.8.2", {"start": v(5.54, 21.68) * mm, "end": v(7.78, 19.44) * mm});
            skLineSegment(sketch, "E7.8.8.3", {"start": v(2.36, 21.68) * mm, "end": v(5.54, 21.68) * mm});
            skLineSegment(sketch, "E7.8.8.4", {"start": v(5.54, 14.02) * mm, "end": v(7.78, 16.26) * mm});
            skLineSegment(sketch, "E7.8.8.5", {"start": v(7.78, 16.26) * mm, "end": v(7.78, 19.44) * mm});
            skLineSegment(sketch, "E7.8.8.6", {"start": v(0.12, 16.26) * mm, "end": v(2.36, 14.02) * mm});
            skLineSegment(sketch, "E7.8.8.7", {"start": v(0.12, 16.26) * mm, "end": v(0.12, 19.44) * mm});
            skLineSegment(sketch, "E7.8.9.0", {"start": v(2.36, 24.18) * mm, "end": v(5.54, 24.18) * mm});
            skLineSegment(sketch, "E7.8.9.1", {"start": v(0.12, 29.6) * mm, "end": v(2.36, 31.84) * mm});
            skLineSegment(sketch, "E7.8.9.2", {"start": v(5.54, 31.84) * mm, "end": v(7.78, 29.6) * mm});
            skLineSegment(sketch, "E7.8.9.3", {"start": v(2.36, 31.84) * mm, "end": v(5.54, 31.84) * mm});
            skLineSegment(sketch, "E7.8.9.4", {"start": v(5.54, 24.18) * mm, "end": v(7.78, 26.42) * mm});
            skLineSegment(sketch, "E7.8.9.5", {"start": v(7.78, 26.42) * mm, "end": v(7.78, 29.6) * mm});
            skLineSegment(sketch, "E7.8.9.6", {"start": v(0.12, 26.42) * mm, "end": v(2.36, 24.18) * mm});
            skLineSegment(sketch, "E7.8.9.7", {"start": v(0.12, 26.42) * mm, "end": v(0.12, 29.6) * mm});
            skLineSegment(sketch, "E7.8.10.0", {"start": v(2.36, 34.34) * mm, "end": v(5.54, 34.34) * mm});
            skLineSegment(sketch, "E7.8.10.1", {"start": v(0.12, 39.76) * mm, "end": v(2.36, 42) * mm});
            skLineSegment(sketch, "E7.8.10.2", {"start": v(5.54, 42) * mm, "end": v(7.78, 39.76) * mm});
            skLineSegment(sketch, "E7.8.10.3", {"start": v(2.36, 42) * mm, "end": v(5.54, 42) * mm});
            skLineSegment(sketch, "E7.8.10.4", {"start": v(5.54, 34.34) * mm, "end": v(7.78, 36.58) * mm});
            skLineSegment(sketch, "E7.8.10.5", {"start": v(7.78, 36.58) * mm, "end": v(7.78, 39.76) * mm});
            skLineSegment(sketch, "E7.8.10.6", {"start": v(0.12, 36.58) * mm, "end": v(2.36, 34.34) * mm});
            skLineSegment(sketch, "E7.8.10.7", {"start": v(0.12, 36.58) * mm, "end": v(0.12, 39.76) * mm});
            skLineSegment(sketch, "E7.8.11.0", {"start": v(2.36, 44.5) * mm, "end": v(5.54, 44.5) * mm});
            skLineSegment(sketch, "E7.8.11.1", {"start": v(0.12, 49.92) * mm, "end": v(2.36, 52.16) * mm});
            skLineSegment(sketch, "E7.8.11.2", {"start": v(5.54, 52.16) * mm, "end": v(7.78, 49.92) * mm});
            skLineSegment(sketch, "E7.8.11.3", {"start": v(2.36, 52.16) * mm, "end": v(5.54, 52.16) * mm});
            skLineSegment(sketch, "E7.8.11.4", {"start": v(5.54, 44.5) * mm, "end": v(7.78, 46.74) * mm});
            skLineSegment(sketch, "E7.8.11.5", {"start": v(7.78, 46.74) * mm, "end": v(7.78, 49.92) * mm});
            skLineSegment(sketch, "E7.8.11.6", {"start": v(0.12, 46.74) * mm, "end": v(2.36, 44.5) * mm});
            skLineSegment(sketch, "E7.8.11.7", {"start": v(0.12, 46.74) * mm, "end": v(0.12, 49.92) * mm});
            skLineSegment(sketch, "E7.8.12.0", {"start": v(2.36, 54.66) * mm, "end": v(5.54, 54.66) * mm});
            skLineSegment(sketch, "E7.8.12.1", {"start": v(0.12, 60.08) * mm, "end": v(2.36, 62.32) * mm});
            skLineSegment(sketch, "E7.8.12.2", {"start": v(5.54, 62.32) * mm, "end": v(7.78, 60.08) * mm});
            skLineSegment(sketch, "E7.8.12.3", {"start": v(2.36, 62.32) * mm, "end": v(5.54, 62.32) * mm});
            skLineSegment(sketch, "E7.8.12.4", {"start": v(5.54, 54.66) * mm, "end": v(7.78, 56.9) * mm});
            skLineSegment(sketch, "E7.8.12.5", {"start": v(7.78, 56.9) * mm, "end": v(7.78, 60.08) * mm});
            skLineSegment(sketch, "E7.8.12.6", {"start": v(0.12, 56.9) * mm, "end": v(2.36, 54.66) * mm});
            skLineSegment(sketch, "E7.8.12.7", {"start": v(0.12, 56.9) * mm, "end": v(0.12, 60.08) * mm});
            skLineSegment(sketch, "E7.8.13.0", {"start": v(2.36, 64.82) * mm, "end": v(5.54, 64.82) * mm});
            skLineSegment(sketch, "E7.8.13.1", {"start": v(0.12, 70.24) * mm, "end": v(0.72, 70.85) * mm});
            skLineSegment(sketch, "E7.8.13.2", {"start": v(7.68, 70.34) * mm, "end": v(7.78, 70.24) * mm});
            skLineSegment(sketch, "E7.8.13.4", {"start": v(5.54, 64.82) * mm, "end": v(7.78, 67.06) * mm});
            skLineSegment(sketch, "E7.8.13.5", {"start": v(7.78, 67.06) * mm, "end": v(7.78, 70.24) * mm});
            skLineSegment(sketch, "E7.8.13.6", {"start": v(0.12, 67.06) * mm, "end": v(2.36, 64.82) * mm});
            skLineSegment(sketch, "E7.8.13.7", {"start": v(0.12, 67.06) * mm, "end": v(0.12, 70.24) * mm});
            skLineSegment(sketch, "E7.9.0.1", {"start": v(9, -61.84) * mm, "end": v(11.25, -59.6) * mm});
            skLineSegment(sketch, "E7.9.0.2", {"start": v(14.43, -59.6) * mm, "end": v(16.67, -61.84) * mm});
            skLineSegment(sketch, "E7.9.0.3", {"start": v(11.25, -59.6) * mm, "end": v(14.43, -59.6) * mm});
            skLineSegment(sketch, "E7.9.1.0", {"start": v(11.25, -57.1) * mm, "end": v(14.43, -57.1) * mm});
            skLineSegment(sketch, "E7.9.1.1", {"start": v(9, -51.68) * mm, "end": v(11.25, -49.44) * mm});
            skLineSegment(sketch, "E7.9.1.2", {"start": v(14.43, -49.44) * mm, "end": v(16.67, -51.68) * mm});
            skLineSegment(sketch, "E7.9.1.3", {"start": v(11.25, -49.44) * mm, "end": v(14.43, -49.44) * mm});
            skLineSegment(sketch, "E7.9.1.4", {"start": v(14.43, -57.1) * mm, "end": v(16.67, -54.86) * mm});
            skLineSegment(sketch, "E7.9.1.5", {"start": v(16.67, -54.86) * mm, "end": v(16.67, -51.68) * mm});
            skLineSegment(sketch, "E7.9.1.6", {"start": v(9, -54.86) * mm, "end": v(11.25, -57.1) * mm});
            skLineSegment(sketch, "E7.9.1.7", {"start": v(9, -54.86) * mm, "end": v(9, -51.68) * mm});
            skLineSegment(sketch, "E7.9.2.0", {"start": v(11.25, -46.94) * mm, "end": v(14.43, -46.94) * mm});
            skLineSegment(sketch, "E7.9.2.1", {"start": v(9, -41.52) * mm, "end": v(11.25, -39.28) * mm});
            skLineSegment(sketch, "E7.9.2.2", {"start": v(14.43, -39.28) * mm, "end": v(16.67, -41.52) * mm});
            skLineSegment(sketch, "E7.9.2.3", {"start": v(11.25, -39.28) * mm, "end": v(14.43, -39.28) * mm});
            skLineSegment(sketch, "E7.9.2.4", {"start": v(14.43, -46.94) * mm, "end": v(16.67, -44.7) * mm});
            skLineSegment(sketch, "E7.9.2.5", {"start": v(16.67, -44.7) * mm, "end": v(16.67, -41.52) * mm});
            skLineSegment(sketch, "E7.9.2.6", {"start": v(9, -44.7) * mm, "end": v(11.25, -46.94) * mm});
            skLineSegment(sketch, "E7.9.2.7", {"start": v(9, -44.7) * mm, "end": v(9, -41.52) * mm});
            skLineSegment(sketch, "E7.9.3.0", {"start": v(11.25, -36.78) * mm, "end": v(14.43, -36.78) * mm});
            skLineSegment(sketch, "E7.9.3.1", {"start": v(9, -31.36) * mm, "end": v(11.25, -29.12) * mm});
            skLineSegment(sketch, "E7.9.3.2", {"start": v(14.43, -29.12) * mm, "end": v(16.67, -31.36) * mm});
            skLineSegment(sketch, "E7.9.3.3", {"start": v(11.25, -29.12) * mm, "end": v(14.43, -29.12) * mm});
            skLineSegment(sketch, "E7.9.3.4", {"start": v(14.43, -36.78) * mm, "end": v(16.67, -34.54) * mm});
            skLineSegment(sketch, "E7.9.3.5", {"start": v(16.67, -34.54) * mm, "end": v(16.67, -31.36) * mm});
            skLineSegment(sketch, "E7.9.3.6", {"start": v(9, -34.54) * mm, "end": v(11.25, -36.78) * mm});
            skLineSegment(sketch, "E7.9.3.7", {"start": v(9, -34.54) * mm, "end": v(9, -31.36) * mm});
            skLineSegment(sketch, "E7.9.4.0", {"start": v(11.25, -26.62) * mm, "end": v(14.43, -26.62) * mm});
            skLineSegment(sketch, "E7.9.4.1", {"start": v(9, -21.2) * mm, "end": v(11.25, -18.96) * mm});
            skLineSegment(sketch, "E7.9.4.2", {"start": v(14.43, -18.96) * mm, "end": v(16.67, -21.2) * mm});
            skLineSegment(sketch, "E7.9.4.3", {"start": v(11.25, -18.96) * mm, "end": v(14.43, -18.96) * mm});
            skLineSegment(sketch, "E7.9.4.4", {"start": v(14.43, -26.62) * mm, "end": v(16.67, -24.38) * mm});
            skLineSegment(sketch, "E7.9.4.5", {"start": v(16.67, -24.38) * mm, "end": v(16.67, -21.2) * mm});
            skLineSegment(sketch, "E7.9.4.6", {"start": v(9, -24.38) * mm, "end": v(11.25, -26.62) * mm});
            skLineSegment(sketch, "E7.9.4.7", {"start": v(9, -24.38) * mm, "end": v(9, -21.2) * mm});
            skLineSegment(sketch, "E7.9.5.0", {"start": v(11.25, -16.46) * mm, "end": v(14.43, -16.46) * mm});
            skLineSegment(sketch, "E7.9.5.1", {"start": v(9, -11.04) * mm, "end": v(11.25, -8.8) * mm});
            skLineSegment(sketch, "E7.9.5.2", {"start": v(14.43, -8.8) * mm, "end": v(16.67, -11.04) * mm});
            skLineSegment(sketch, "E7.9.5.3", {"start": v(11.25, -8.8) * mm, "end": v(14.43, -8.8) * mm});
            skLineSegment(sketch, "E7.9.5.4", {"start": v(14.43, -16.46) * mm, "end": v(16.67, -14.22) * mm});
            skLineSegment(sketch, "E7.9.5.5", {"start": v(16.67, -14.22) * mm, "end": v(16.67, -11.04) * mm});
            skLineSegment(sketch, "E7.9.5.6", {"start": v(9, -14.22) * mm, "end": v(11.25, -16.46) * mm});
            skLineSegment(sketch, "E7.9.5.7", {"start": v(9, -14.22) * mm, "end": v(9, -11.04) * mm});
            skLineSegment(sketch, "E7.9.6.0", {"start": v(11.25, -6.3) * mm, "end": v(14.43, -6.3) * mm});
            skLineSegment(sketch, "E7.9.6.1", {"start": v(9, -0.88) * mm, "end": v(11.25, 1.36) * mm});
            skLineSegment(sketch, "E7.9.6.2", {"start": v(14.43, 1.36) * mm, "end": v(16.67, -0.88) * mm});
            skLineSegment(sketch, "E7.9.6.3", {"start": v(11.25, 1.36) * mm, "end": v(14.43, 1.36) * mm});
            skLineSegment(sketch, "E7.9.6.4", {"start": v(14.43, -6.3) * mm, "end": v(16.67, -4.06) * mm});
            skLineSegment(sketch, "E7.9.6.5", {"start": v(16.67, -4.06) * mm, "end": v(16.67, -0.88) * mm});
            skLineSegment(sketch, "E7.9.6.6", {"start": v(9, -4.06) * mm, "end": v(11.25, -6.3) * mm});
            skLineSegment(sketch, "E7.9.6.7", {"start": v(9, -4.06) * mm, "end": v(9, -0.88) * mm});
            skLineSegment(sketch, "E7.9.7.0", {"start": v(11.25, 3.86) * mm, "end": v(14.43, 3.86) * mm});
            skLineSegment(sketch, "E7.9.7.1", {"start": v(9, 9.28) * mm, "end": v(11.25, 11.52) * mm});
            skLineSegment(sketch, "E7.9.7.2", {"start": v(14.43, 11.52) * mm, "end": v(16.67, 9.28) * mm});
            skLineSegment(sketch, "E7.9.7.3", {"start": v(11.25, 11.52) * mm, "end": v(14.43, 11.52) * mm});
            skLineSegment(sketch, "E7.9.7.4", {"start": v(14.43, 3.86) * mm, "end": v(16.67, 6.1) * mm});
            skLineSegment(sketch, "E7.9.7.5", {"start": v(16.67, 6.1) * mm, "end": v(16.67, 9.28) * mm});
            skLineSegment(sketch, "E7.9.7.6", {"start": v(9, 6.1) * mm, "end": v(11.25, 3.86) * mm});
            skLineSegment(sketch, "E7.9.7.7", {"start": v(9, 6.1) * mm, "end": v(9, 9.28) * mm});
            skLineSegment(sketch, "E7.9.8.0", {"start": v(11.25, 14.02) * mm, "end": v(14.43, 14.02) * mm});
            skLineSegment(sketch, "E7.9.8.1", {"start": v(9, 19.44) * mm, "end": v(11.25, 21.68) * mm});
            skLineSegment(sketch, "E7.9.8.2", {"start": v(14.43, 21.68) * mm, "end": v(16.67, 19.44) * mm});
            skLineSegment(sketch, "E7.9.8.3", {"start": v(11.25, 21.68) * mm, "end": v(14.43, 21.68) * mm});
            skLineSegment(sketch, "E7.9.8.4", {"start": v(14.43, 14.02) * mm, "end": v(16.67, 16.26) * mm});
            skLineSegment(sketch, "E7.9.8.5", {"start": v(16.67, 16.26) * mm, "end": v(16.67, 19.44) * mm});
            skLineSegment(sketch, "E7.9.8.6", {"start": v(9, 16.26) * mm, "end": v(11.25, 14.02) * mm});
            skLineSegment(sketch, "E7.9.8.7", {"start": v(9, 16.26) * mm, "end": v(9, 19.44) * mm});
            skLineSegment(sketch, "E7.9.9.0", {"start": v(11.25, 24.18) * mm, "end": v(14.43, 24.18) * mm});
            skLineSegment(sketch, "E7.9.9.1", {"start": v(9, 29.6) * mm, "end": v(11.25, 31.84) * mm});
            skLineSegment(sketch, "E7.9.9.2", {"start": v(14.43, 31.84) * mm, "end": v(16.67, 29.6) * mm});
            skLineSegment(sketch, "E7.9.9.3", {"start": v(11.25, 31.84) * mm, "end": v(14.43, 31.84) * mm});
            skLineSegment(sketch, "E7.9.9.4", {"start": v(14.43, 24.18) * mm, "end": v(16.67, 26.42) * mm});
            skLineSegment(sketch, "E7.9.9.5", {"start": v(16.67, 26.42) * mm, "end": v(16.67, 29.6) * mm});
            skLineSegment(sketch, "E7.9.9.6", {"start": v(9, 26.42) * mm, "end": v(11.25, 24.18) * mm});
            skLineSegment(sketch, "E7.9.9.7", {"start": v(9, 26.42) * mm, "end": v(9, 29.6) * mm});
            skLineSegment(sketch, "E7.9.10.0", {"start": v(11.25, 34.34) * mm, "end": v(14.43, 34.34) * mm});
            skLineSegment(sketch, "E7.9.10.1", {"start": v(9, 39.76) * mm, "end": v(11.25, 42) * mm});
            skLineSegment(sketch, "E7.9.10.2", {"start": v(14.43, 42) * mm, "end": v(16.67, 39.76) * mm});
            skLineSegment(sketch, "E7.9.10.3", {"start": v(11.25, 42) * mm, "end": v(14.43, 42) * mm});
            skLineSegment(sketch, "E7.9.10.4", {"start": v(14.43, 34.34) * mm, "end": v(16.67, 36.58) * mm});
            skLineSegment(sketch, "E7.9.10.5", {"start": v(16.67, 36.58) * mm, "end": v(16.67, 39.76) * mm});
            skLineSegment(sketch, "E7.9.10.6", {"start": v(9, 36.58) * mm, "end": v(11.25, 34.34) * mm});
            skLineSegment(sketch, "E7.9.10.7", {"start": v(9, 36.58) * mm, "end": v(9, 39.76) * mm});
            skLineSegment(sketch, "E7.9.11.0", {"start": v(11.25, 44.5) * mm, "end": v(14.43, 44.5) * mm});
            skLineSegment(sketch, "E7.9.11.1", {"start": v(9, 49.92) * mm, "end": v(11.25, 52.16) * mm});
            skLineSegment(sketch, "E7.9.11.2", {"start": v(14.43, 52.16) * mm, "end": v(16.67, 49.92) * mm});
            skLineSegment(sketch, "E7.9.11.3", {"start": v(11.25, 52.16) * mm, "end": v(14.43, 52.16) * mm});
            skLineSegment(sketch, "E7.9.11.4", {"start": v(14.43, 44.5) * mm, "end": v(16.67, 46.74) * mm});
            skLineSegment(sketch, "E7.9.11.5", {"start": v(16.67, 46.74) * mm, "end": v(16.67, 49.92) * mm});
            skLineSegment(sketch, "E7.9.11.6", {"start": v(9, 46.74) * mm, "end": v(11.25, 44.5) * mm});
            skLineSegment(sketch, "E7.9.11.7", {"start": v(9, 46.74) * mm, "end": v(9, 49.92) * mm});
            skLineSegment(sketch, "E7.9.12.0", {"start": v(11.25, 54.66) * mm, "end": v(14.43, 54.66) * mm});
            skLineSegment(sketch, "E7.9.12.1", {"start": v(9, 60.08) * mm, "end": v(11.25, 62.32) * mm});
            skLineSegment(sketch, "E7.9.12.2", {"start": v(14.43, 62.32) * mm, "end": v(16.67, 60.08) * mm});
            skLineSegment(sketch, "E7.9.12.3", {"start": v(11.25, 62.32) * mm, "end": v(14.43, 62.32) * mm});
            skLineSegment(sketch, "E7.9.12.4", {"start": v(14.43, 54.66) * mm, "end": v(16.67, 56.9) * mm});
            skLineSegment(sketch, "E7.9.12.5", {"start": v(16.67, 56.9) * mm, "end": v(16.67, 60.08) * mm});
            skLineSegment(sketch, "E7.9.12.6", {"start": v(9, 56.9) * mm, "end": v(11.25, 54.66) * mm});
            skLineSegment(sketch, "E7.9.12.7", {"start": v(9, 56.9) * mm, "end": v(9, 60.08) * mm});
            skLineSegment(sketch, "E7.9.13.0", {"start": v(11.25, 64.82) * mm, "end": v(14.43, 64.82) * mm});
            skLineSegment(sketch, "E7.9.13.4", {"start": v(14.43, 64.82) * mm, "end": v(16.67, 67.06) * mm});
            skLineSegment(sketch, "E7.9.13.5", {"start": v(16.67, 67.06) * mm, "end": v(16.67, 68.4) * mm});
            skLineSegment(sketch, "E7.9.13.6", {"start": v(9, 67.06) * mm, "end": v(11.25, 64.82) * mm});
            skLineSegment(sketch, "E7.9.13.7", {"start": v(9, 67.06) * mm, "end": v(9, 70.15) * mm});
            skLineSegment(sketch, "E7.10.0.1", {"start": v(17.9, -61.84) * mm, "end": v(20.14, -59.6) * mm});
            skLineSegment(sketch, "E7.10.0.2", {"start": v(23.32, -59.6) * mm, "end": v(25.56, -61.84) * mm});
            skLineSegment(sketch, "E7.10.0.3", {"start": v(20.14, -59.6) * mm, "end": v(23.32, -59.6) * mm});
            skLineSegment(sketch, "E7.10.1.0", {"start": v(20.14, -57.1) * mm, "end": v(23.32, -57.1) * mm});
            skLineSegment(sketch, "E7.10.1.1", {"start": v(17.9, -51.68) * mm, "end": v(20.14, -49.44) * mm});
            skLineSegment(sketch, "E7.10.1.2", {"start": v(23.32, -49.44) * mm, "end": v(25.56, -51.68) * mm});
            skLineSegment(sketch, "E7.10.1.3", {"start": v(20.14, -49.44) * mm, "end": v(23.32, -49.44) * mm});
            skLineSegment(sketch, "E7.10.1.4", {"start": v(23.32, -57.1) * mm, "end": v(25.56, -54.86) * mm});
            skLineSegment(sketch, "E7.10.1.5", {"start": v(25.56, -54.86) * mm, "end": v(25.56, -51.68) * mm});
            skLineSegment(sketch, "E7.10.1.6", {"start": v(17.9, -54.86) * mm, "end": v(20.14, -57.1) * mm});
            skLineSegment(sketch, "E7.10.1.7", {"start": v(17.9, -54.86) * mm, "end": v(17.9, -51.68) * mm});
            skLineSegment(sketch, "E7.10.2.0", {"start": v(20.14, -46.94) * mm, "end": v(23.32, -46.94) * mm});
            skLineSegment(sketch, "E7.10.2.1", {"start": v(17.9, -41.52) * mm, "end": v(20.14, -39.28) * mm});
            skLineSegment(sketch, "E7.10.2.2", {"start": v(23.32, -39.28) * mm, "end": v(25.56, -41.52) * mm});
            skLineSegment(sketch, "E7.10.2.3", {"start": v(20.14, -39.28) * mm, "end": v(23.32, -39.28) * mm});
            skLineSegment(sketch, "E7.10.2.4", {"start": v(23.32, -46.94) * mm, "end": v(25.56, -44.7) * mm});
            skLineSegment(sketch, "E7.10.2.5", {"start": v(25.56, -44.7) * mm, "end": v(25.56, -41.52) * mm});
            skLineSegment(sketch, "E7.10.2.6", {"start": v(17.9, -44.7) * mm, "end": v(20.14, -46.94) * mm});
            skLineSegment(sketch, "E7.10.2.7", {"start": v(17.9, -44.7) * mm, "end": v(17.9, -41.52) * mm});
            skLineSegment(sketch, "E7.10.3.0", {"start": v(20.14, -36.78) * mm, "end": v(23.32, -36.78) * mm});
            skLineSegment(sketch, "E7.10.3.1", {"start": v(17.9, -31.36) * mm, "end": v(20.14, -29.12) * mm});
            skLineSegment(sketch, "E7.10.3.2", {"start": v(23.32, -29.12) * mm, "end": v(25.56, -31.36) * mm});
            skLineSegment(sketch, "E7.10.3.3", {"start": v(20.14, -29.12) * mm, "end": v(23.32, -29.12) * mm});
            skLineSegment(sketch, "E7.10.3.4", {"start": v(23.32, -36.78) * mm, "end": v(25.56, -34.54) * mm});
            skLineSegment(sketch, "E7.10.3.5", {"start": v(25.56, -34.54) * mm, "end": v(25.56, -31.36) * mm});
            skLineSegment(sketch, "E7.10.3.6", {"start": v(17.9, -34.54) * mm, "end": v(20.14, -36.78) * mm});
            skLineSegment(sketch, "E7.10.3.7", {"start": v(17.9, -34.54) * mm, "end": v(17.9, -31.36) * mm});
            skLineSegment(sketch, "E7.10.4.0", {"start": v(20.14, -26.62) * mm, "end": v(23.32, -26.62) * mm});
            skLineSegment(sketch, "E7.10.4.1", {"start": v(17.9, -21.2) * mm, "end": v(20.14, -18.96) * mm});
            skLineSegment(sketch, "E7.10.4.2", {"start": v(23.32, -18.96) * mm, "end": v(25.56, -21.2) * mm});
            skLineSegment(sketch, "E7.10.4.3", {"start": v(20.14, -18.96) * mm, "end": v(23.32, -18.96) * mm});
            skLineSegment(sketch, "E7.10.4.4", {"start": v(23.32, -26.62) * mm, "end": v(25.56, -24.38) * mm});
            skLineSegment(sketch, "E7.10.4.5", {"start": v(25.56, -24.38) * mm, "end": v(25.56, -21.2) * mm});
            skLineSegment(sketch, "E7.10.4.6", {"start": v(17.9, -24.38) * mm, "end": v(20.14, -26.62) * mm});
            skLineSegment(sketch, "E7.10.4.7", {"start": v(17.9, -24.38) * mm, "end": v(17.9, -21.2) * mm});
            skLineSegment(sketch, "E7.10.5.0", {"start": v(20.14, -16.46) * mm, "end": v(23.32, -16.46) * mm});
            skLineSegment(sketch, "E7.10.5.1", {"start": v(17.9, -11.04) * mm, "end": v(20.14, -8.8) * mm});
            skLineSegment(sketch, "E7.10.5.2", {"start": v(23.32, -8.8) * mm, "end": v(25.56, -11.04) * mm});
            skLineSegment(sketch, "E7.10.5.3", {"start": v(20.14, -8.8) * mm, "end": v(23.32, -8.8) * mm});
            skLineSegment(sketch, "E7.10.5.4", {"start": v(23.32, -16.46) * mm, "end": v(25.56, -14.22) * mm});
            skLineSegment(sketch, "E7.10.5.5", {"start": v(25.56, -14.22) * mm, "end": v(25.56, -11.04) * mm});
            skLineSegment(sketch, "E7.10.5.6", {"start": v(17.9, -14.22) * mm, "end": v(20.14, -16.46) * mm});
            skLineSegment(sketch, "E7.10.5.7", {"start": v(17.9, -14.22) * mm, "end": v(17.9, -11.04) * mm});
            skLineSegment(sketch, "E7.10.6.0", {"start": v(20.14, -6.3) * mm, "end": v(23.32, -6.3) * mm});
            skLineSegment(sketch, "E7.10.6.1", {"start": v(17.9, -0.88) * mm, "end": v(20.14, 1.36) * mm});
            skLineSegment(sketch, "E7.10.6.2", {"start": v(23.32, 1.36) * mm, "end": v(25.56, -0.88) * mm});
            skLineSegment(sketch, "E7.10.6.3", {"start": v(20.14, 1.36) * mm, "end": v(23.32, 1.36) * mm});
            skLineSegment(sketch, "E7.10.6.4", {"start": v(23.32, -6.3) * mm, "end": v(25.56, -4.06) * mm});
            skLineSegment(sketch, "E7.10.6.5", {"start": v(25.56, -4.06) * mm, "end": v(25.56, -0.88) * mm});
            skLineSegment(sketch, "E7.10.6.6", {"start": v(17.9, -4.06) * mm, "end": v(20.14, -6.3) * mm});
            skLineSegment(sketch, "E7.10.6.7", {"start": v(17.9, -4.06) * mm, "end": v(17.9, -0.88) * mm});
            skLineSegment(sketch, "E7.10.7.0", {"start": v(20.14, 3.86) * mm, "end": v(23.32, 3.86) * mm});
            skLineSegment(sketch, "E7.10.7.1", {"start": v(17.9, 9.28) * mm, "end": v(20.14, 11.52) * mm});
            skLineSegment(sketch, "E7.10.7.2", {"start": v(23.32, 11.52) * mm, "end": v(25.56, 9.28) * mm});
            skLineSegment(sketch, "E7.10.7.3", {"start": v(20.14, 11.52) * mm, "end": v(23.32, 11.52) * mm});
            skLineSegment(sketch, "E7.10.7.4", {"start": v(23.32, 3.86) * mm, "end": v(25.56, 6.1) * mm});
            skLineSegment(sketch, "E7.10.7.5", {"start": v(25.56, 6.1) * mm, "end": v(25.56, 9.28) * mm});
            skLineSegment(sketch, "E7.10.7.6", {"start": v(17.9, 6.1) * mm, "end": v(20.14, 3.86) * mm});
            skLineSegment(sketch, "E7.10.7.7", {"start": v(17.9, 6.1) * mm, "end": v(17.9, 9.28) * mm});
            skLineSegment(sketch, "E7.10.8.0", {"start": v(20.14, 14.02) * mm, "end": v(23.32, 14.02) * mm});
            skLineSegment(sketch, "E7.10.8.1", {"start": v(17.9, 19.44) * mm, "end": v(20.14, 21.68) * mm});
            skLineSegment(sketch, "E7.10.8.2", {"start": v(23.32, 21.68) * mm, "end": v(25.56, 19.44) * mm});
            skLineSegment(sketch, "E7.10.8.3", {"start": v(20.14, 21.68) * mm, "end": v(23.32, 21.68) * mm});
            skLineSegment(sketch, "E7.10.8.4", {"start": v(23.32, 14.02) * mm, "end": v(25.56, 16.26) * mm});
            skLineSegment(sketch, "E7.10.8.5", {"start": v(25.56, 16.26) * mm, "end": v(25.56, 19.44) * mm});
            skLineSegment(sketch, "E7.10.8.6", {"start": v(17.9, 16.26) * mm, "end": v(20.14, 14.02) * mm});
            skLineSegment(sketch, "E7.10.8.7", {"start": v(17.9, 16.26) * mm, "end": v(17.9, 19.44) * mm});
            skLineSegment(sketch, "E7.10.9.0", {"start": v(20.14, 24.18) * mm, "end": v(23.32, 24.18) * mm});
            skLineSegment(sketch, "E7.10.9.1", {"start": v(17.9, 29.6) * mm, "end": v(20.14, 31.84) * mm});
            skLineSegment(sketch, "E7.10.9.2", {"start": v(23.32, 31.84) * mm, "end": v(25.56, 29.6) * mm});
            skLineSegment(sketch, "E7.10.9.3", {"start": v(20.14, 31.84) * mm, "end": v(23.32, 31.84) * mm});
            skLineSegment(sketch, "E7.10.9.4", {"start": v(23.32, 24.18) * mm, "end": v(25.56, 26.42) * mm});
            skLineSegment(sketch, "E7.10.9.5", {"start": v(25.56, 26.42) * mm, "end": v(25.56, 29.6) * mm});
            skLineSegment(sketch, "E7.10.9.6", {"start": v(17.9, 26.42) * mm, "end": v(20.14, 24.18) * mm});
            skLineSegment(sketch, "E7.10.9.7", {"start": v(17.9, 26.42) * mm, "end": v(17.9, 29.6) * mm});
            skLineSegment(sketch, "E7.10.10.0", {"start": v(20.14, 34.34) * mm, "end": v(23.32, 34.34) * mm});
            skLineSegment(sketch, "E7.10.10.1", {"start": v(17.9, 39.76) * mm, "end": v(20.14, 42) * mm});
            skLineSegment(sketch, "E7.10.10.2", {"start": v(23.32, 42) * mm, "end": v(25.56, 39.76) * mm});
            skLineSegment(sketch, "E7.10.10.3", {"start": v(20.14, 42) * mm, "end": v(23.32, 42) * mm});
            skLineSegment(sketch, "E7.10.10.4", {"start": v(23.32, 34.34) * mm, "end": v(25.56, 36.58) * mm});
            skLineSegment(sketch, "E7.10.10.5", {"start": v(25.56, 36.58) * mm, "end": v(25.56, 39.76) * mm});
            skLineSegment(sketch, "E7.10.10.6", {"start": v(17.9, 36.58) * mm, "end": v(20.14, 34.34) * mm});
            skLineSegment(sketch, "E7.10.10.7", {"start": v(17.9, 36.58) * mm, "end": v(17.9, 39.76) * mm});
            skLineSegment(sketch, "E7.10.11.0", {"start": v(20.14, 44.5) * mm, "end": v(23.32, 44.5) * mm});
            skLineSegment(sketch, "E7.10.11.1", {"start": v(17.9, 49.92) * mm, "end": v(20.14, 52.16) * mm});
            skLineSegment(sketch, "E7.10.11.2", {"start": v(23.32, 52.16) * mm, "end": v(25.56, 49.92) * mm});
            skLineSegment(sketch, "E7.10.11.3", {"start": v(20.14, 52.16) * mm, "end": v(23.32, 52.16) * mm});
            skLineSegment(sketch, "E7.10.11.4", {"start": v(23.32, 44.5) * mm, "end": v(25.56, 46.74) * mm});
            skLineSegment(sketch, "E7.10.11.5", {"start": v(25.56, 46.74) * mm, "end": v(25.56, 49.92) * mm});
            skLineSegment(sketch, "E7.10.11.6", {"start": v(17.9, 46.74) * mm, "end": v(20.14, 44.5) * mm});
            skLineSegment(sketch, "E7.10.11.7", {"start": v(17.9, 46.74) * mm, "end": v(17.9, 49.92) * mm});
            skLineSegment(sketch, "E7.10.12.0", {"start": v(20.14, 54.66) * mm, "end": v(23.32, 54.66) * mm});
            skLineSegment(sketch, "E7.10.12.1", {"start": v(17.9, 60.08) * mm, "end": v(20.14, 62.32) * mm});
            skLineSegment(sketch, "E7.10.12.2", {"start": v(23.32, 62.32) * mm, "end": v(25.56, 60.08) * mm});
            skLineSegment(sketch, "E7.10.12.3", {"start": v(20.14, 62.32) * mm, "end": v(23.32, 62.32) * mm});
            skLineSegment(sketch, "E7.10.12.4", {"start": v(23.32, 54.66) * mm, "end": v(25.56, 56.9) * mm});
            skLineSegment(sketch, "E7.10.12.5", {"start": v(25.56, 56.9) * mm, "end": v(25.56, 60.08) * mm});
            skLineSegment(sketch, "E7.10.12.6", {"start": v(17.9, 56.9) * mm, "end": v(20.14, 54.66) * mm});
            skLineSegment(sketch, "E7.10.12.7", {"start": v(17.9, 56.9) * mm, "end": v(17.9, 60.08) * mm});
            skLineSegment(sketch, "E7.10.13.0", {"start": v(20.14, 64.82) * mm, "end": v(23.32, 64.82) * mm});
            skLineSegment(sketch, "E7.10.13.4", {"start": v(23.32, 64.82) * mm, "end": v(24.1, 65.6) * mm});
            skLineSegment(sketch, "E7.10.13.6", {"start": v(17.9, 67.06) * mm, "end": v(20.14, 64.82) * mm});
            skLineSegment(sketch, "E7.10.13.7", {"start": v(17.9, 67.06) * mm, "end": v(17.9, 68.02) * mm});
            skLineSegment(sketch, "E7.11.0.1", {"start": v(26.79, -61.84) * mm, "end": v(29.03, -59.6) * mm});
            skLineSegment(sketch, "E7.11.0.2", {"start": v(32.2, -59.6) * mm, "end": v(34.45, -61.84) * mm});
            skLineSegment(sketch, "E7.11.0.3", {"start": v(29.03, -59.6) * mm, "end": v(32.2, -59.6) * mm});
            skLineSegment(sketch, "E7.11.1.0", {"start": v(29.03, -57.1) * mm, "end": v(32.2, -57.1) * mm});
            skLineSegment(sketch, "E7.11.1.1", {"start": v(26.79, -51.68) * mm, "end": v(29.03, -49.44) * mm});
            skLineSegment(sketch, "E7.11.1.2", {"start": v(32.2, -49.44) * mm, "end": v(34.45, -51.68) * mm});
            skLineSegment(sketch, "E7.11.1.3", {"start": v(29.03, -49.44) * mm, "end": v(32.2, -49.44) * mm});
            skLineSegment(sketch, "E7.11.1.4", {"start": v(32.2, -57.1) * mm, "end": v(34.45, -54.86) * mm});
            skLineSegment(sketch, "E7.11.1.5", {"start": v(34.45, -54.86) * mm, "end": v(34.45, -51.68) * mm});
            skLineSegment(sketch, "E7.11.1.6", {"start": v(26.79, -54.86) * mm, "end": v(29.03, -57.1) * mm});
            skLineSegment(sketch, "E7.11.1.7", {"start": v(26.79, -54.86) * mm, "end": v(26.79, -51.68) * mm});
            skLineSegment(sketch, "E7.11.2.0", {"start": v(29.03, -46.94) * mm, "end": v(32.2, -46.94) * mm});
            skLineSegment(sketch, "E7.11.2.1", {"start": v(26.79, -41.52) * mm, "end": v(29.03, -39.28) * mm});
            skLineSegment(sketch, "E7.11.2.2", {"start": v(32.2, -39.28) * mm, "end": v(34.45, -41.52) * mm});
            skLineSegment(sketch, "E7.11.2.3", {"start": v(29.03, -39.28) * mm, "end": v(32.2, -39.28) * mm});
            skLineSegment(sketch, "E7.11.2.4", {"start": v(32.2, -46.94) * mm, "end": v(34.45, -44.7) * mm});
            skLineSegment(sketch, "E7.11.2.5", {"start": v(34.45, -44.7) * mm, "end": v(34.45, -41.52) * mm});
            skLineSegment(sketch, "E7.11.2.6", {"start": v(26.79, -44.7) * mm, "end": v(29.03, -46.94) * mm});
            skLineSegment(sketch, "E7.11.2.7", {"start": v(26.79, -44.7) * mm, "end": v(26.79, -41.52) * mm});
            skLineSegment(sketch, "E7.11.3.0", {"start": v(29.03, -36.78) * mm, "end": v(32.2, -36.78) * mm});
            skLineSegment(sketch, "E7.11.3.1", {"start": v(26.79, -31.36) * mm, "end": v(29.03, -29.12) * mm});
            skLineSegment(sketch, "E7.11.3.2", {"start": v(32.2, -29.12) * mm, "end": v(34.45, -31.36) * mm});
            skLineSegment(sketch, "E7.11.3.3", {"start": v(29.03, -29.12) * mm, "end": v(32.2, -29.12) * mm});
            skLineSegment(sketch, "E7.11.3.4", {"start": v(32.2, -36.78) * mm, "end": v(34.45, -34.54) * mm});
            skLineSegment(sketch, "E7.11.3.5", {"start": v(34.45, -34.54) * mm, "end": v(34.45, -31.36) * mm});
            skLineSegment(sketch, "E7.11.3.6", {"start": v(26.79, -34.54) * mm, "end": v(29.03, -36.78) * mm});
            skLineSegment(sketch, "E7.11.3.7", {"start": v(26.79, -34.54) * mm, "end": v(26.79, -31.36) * mm});
            skLineSegment(sketch, "E7.11.4.0", {"start": v(29.03, -26.62) * mm, "end": v(32.2, -26.62) * mm});
            skLineSegment(sketch, "E7.11.4.1", {"start": v(26.79, -21.2) * mm, "end": v(29.03, -18.96) * mm});
            skLineSegment(sketch, "E7.11.4.2", {"start": v(32.2, -18.96) * mm, "end": v(34.45, -21.2) * mm});
            skLineSegment(sketch, "E7.11.4.3", {"start": v(29.03, -18.96) * mm, "end": v(32.2, -18.96) * mm});
            skLineSegment(sketch, "E7.11.4.4", {"start": v(32.2, -26.62) * mm, "end": v(34.45, -24.38) * mm});
            skLineSegment(sketch, "E7.11.4.5", {"start": v(34.45, -24.38) * mm, "end": v(34.45, -21.2) * mm});
            skLineSegment(sketch, "E7.11.4.6", {"start": v(26.79, -24.38) * mm, "end": v(29.03, -26.62) * mm});
            skLineSegment(sketch, "E7.11.4.7", {"start": v(26.79, -24.38) * mm, "end": v(26.79, -21.2) * mm});
            skLineSegment(sketch, "E7.11.5.0", {"start": v(29.03, -16.46) * mm, "end": v(32.2, -16.46) * mm});
            skLineSegment(sketch, "E7.11.5.1", {"start": v(26.79, -11.04) * mm, "end": v(29.03, -8.8) * mm});
            skLineSegment(sketch, "E7.11.5.2", {"start": v(32.2, -8.8) * mm, "end": v(34.45, -11.04) * mm});
            skLineSegment(sketch, "E7.11.5.3", {"start": v(29.03, -8.8) * mm, "end": v(32.2, -8.8) * mm});
            skLineSegment(sketch, "E7.11.5.4", {"start": v(32.2, -16.46) * mm, "end": v(34.45, -14.22) * mm});
            skLineSegment(sketch, "E7.11.5.5", {"start": v(34.45, -14.22) * mm, "end": v(34.45, -11.04) * mm});
            skLineSegment(sketch, "E7.11.5.6", {"start": v(26.79, -14.22) * mm, "end": v(29.03, -16.46) * mm});
            skLineSegment(sketch, "E7.11.5.7", {"start": v(26.79, -14.22) * mm, "end": v(26.79, -11.04) * mm});
            skLineSegment(sketch, "E7.11.6.0", {"start": v(29.03, -6.3) * mm, "end": v(32.2, -6.3) * mm});
            skLineSegment(sketch, "E7.11.6.1", {"start": v(26.79, -0.88) * mm, "end": v(29.03, 1.36) * mm});
            skLineSegment(sketch, "E7.11.6.2", {"start": v(32.2, 1.36) * mm, "end": v(34.45, -0.88) * mm});
            skLineSegment(sketch, "E7.11.6.3", {"start": v(29.03, 1.36) * mm, "end": v(32.2, 1.36) * mm});
            skLineSegment(sketch, "E7.11.6.4", {"start": v(32.2, -6.3) * mm, "end": v(34.45, -4.06) * mm});
            skLineSegment(sketch, "E7.11.6.5", {"start": v(34.45, -4.06) * mm, "end": v(34.45, -0.88) * mm});
            skLineSegment(sketch, "E7.11.6.6", {"start": v(26.79, -4.06) * mm, "end": v(29.03, -6.3) * mm});
            skLineSegment(sketch, "E7.11.6.7", {"start": v(26.79, -4.06) * mm, "end": v(26.79, -0.88) * mm});
            skLineSegment(sketch, "E7.11.7.0", {"start": v(29.03, 3.86) * mm, "end": v(32.2, 3.86) * mm});
            skLineSegment(sketch, "E7.11.7.1", {"start": v(26.79, 9.28) * mm, "end": v(29.03, 11.52) * mm});
            skLineSegment(sketch, "E7.11.7.2", {"start": v(32.2, 11.52) * mm, "end": v(34.45, 9.28) * mm});
            skLineSegment(sketch, "E7.11.7.3", {"start": v(29.03, 11.52) * mm, "end": v(32.2, 11.52) * mm});
            skLineSegment(sketch, "E7.11.7.4", {"start": v(32.2, 3.86) * mm, "end": v(34.45, 6.1) * mm});
            skLineSegment(sketch, "E7.11.7.5", {"start": v(34.45, 6.1) * mm, "end": v(34.45, 9.28) * mm});
            skLineSegment(sketch, "E7.11.7.6", {"start": v(26.79, 6.1) * mm, "end": v(29.03, 3.86) * mm});
            skLineSegment(sketch, "E7.11.7.7", {"start": v(26.79, 6.1) * mm, "end": v(26.79, 9.28) * mm});
            skLineSegment(sketch, "E7.11.8.0", {"start": v(29.03, 14.02) * mm, "end": v(32.2, 14.02) * mm});
            skLineSegment(sketch, "E7.11.8.1", {"start": v(26.79, 19.44) * mm, "end": v(29.03, 21.68) * mm});
            skLineSegment(sketch, "E7.11.8.2", {"start": v(32.2, 21.68) * mm, "end": v(34.45, 19.44) * mm});
            skLineSegment(sketch, "E7.11.8.3", {"start": v(29.03, 21.68) * mm, "end": v(32.2, 21.68) * mm});
            skLineSegment(sketch, "E7.11.8.4", {"start": v(32.2, 14.02) * mm, "end": v(34.45, 16.26) * mm});
            skLineSegment(sketch, "E7.11.8.5", {"start": v(34.45, 16.26) * mm, "end": v(34.45, 19.44) * mm});
            skLineSegment(sketch, "E7.11.8.6", {"start": v(26.79, 16.26) * mm, "end": v(29.03, 14.02) * mm});
            skLineSegment(sketch, "E7.11.8.7", {"start": v(26.79, 16.26) * mm, "end": v(26.79, 19.44) * mm});
            skLineSegment(sketch, "E7.11.9.0", {"start": v(29.03, 24.18) * mm, "end": v(32.2, 24.18) * mm});
            skLineSegment(sketch, "E7.11.9.1", {"start": v(26.79, 29.6) * mm, "end": v(29.03, 31.84) * mm});
            skLineSegment(sketch, "E7.11.9.2", {"start": v(32.2, 31.84) * mm, "end": v(34.45, 29.6) * mm});
            skLineSegment(sketch, "E7.11.9.3", {"start": v(29.03, 31.84) * mm, "end": v(32.2, 31.84) * mm});
            skLineSegment(sketch, "E7.11.9.4", {"start": v(32.2, 24.18) * mm, "end": v(34.45, 26.42) * mm});
            skLineSegment(sketch, "E7.11.9.5", {"start": v(34.45, 26.42) * mm, "end": v(34.45, 29.6) * mm});
            skLineSegment(sketch, "E7.11.9.6", {"start": v(26.79, 26.42) * mm, "end": v(29.03, 24.18) * mm});
            skLineSegment(sketch, "E7.11.9.7", {"start": v(26.79, 26.42) * mm, "end": v(26.79, 29.6) * mm});
            skLineSegment(sketch, "E7.11.10.0", {"start": v(29.03, 34.34) * mm, "end": v(32.2, 34.34) * mm});
            skLineSegment(sketch, "E7.11.10.1", {"start": v(26.79, 39.76) * mm, "end": v(29.03, 42) * mm});
            skLineSegment(sketch, "E7.11.10.2", {"start": v(32.2, 42) * mm, "end": v(34.45, 39.76) * mm});
            skLineSegment(sketch, "E7.11.10.3", {"start": v(29.03, 42) * mm, "end": v(32.2, 42) * mm});
            skLineSegment(sketch, "E7.11.10.4", {"start": v(32.2, 34.34) * mm, "end": v(34.45, 36.58) * mm});
            skLineSegment(sketch, "E7.11.10.5", {"start": v(34.45, 36.58) * mm, "end": v(34.45, 39.76) * mm});
            skLineSegment(sketch, "E7.11.10.6", {"start": v(26.79, 36.58) * mm, "end": v(29.03, 34.34) * mm});
            skLineSegment(sketch, "E7.11.10.7", {"start": v(26.79, 36.58) * mm, "end": v(26.79, 39.76) * mm});
            skLineSegment(sketch, "E7.11.11.0", {"start": v(29.03, 44.5) * mm, "end": v(32.2, 44.5) * mm});
            skLineSegment(sketch, "E7.11.11.1", {"start": v(26.79, 49.92) * mm, "end": v(29.03, 52.16) * mm});
            skLineSegment(sketch, "E7.11.11.2", {"start": v(32.2, 52.16) * mm, "end": v(34.45, 49.92) * mm});
            skLineSegment(sketch, "E7.11.11.3", {"start": v(29.03, 52.16) * mm, "end": v(32.2, 52.16) * mm});
            skLineSegment(sketch, "E7.11.11.4", {"start": v(32.2, 44.5) * mm, "end": v(34.45, 46.74) * mm});
            skLineSegment(sketch, "E7.11.11.5", {"start": v(34.45, 46.74) * mm, "end": v(34.45, 49.92) * mm});
            skLineSegment(sketch, "E7.11.11.6", {"start": v(26.79, 46.74) * mm, "end": v(29.03, 44.5) * mm});
            skLineSegment(sketch, "E7.11.11.7", {"start": v(26.79, 46.74) * mm, "end": v(26.79, 49.92) * mm});
            skLineSegment(sketch, "E7.11.12.0", {"start": v(29.03, 54.66) * mm, "end": v(32.2, 54.66) * mm});
            skLineSegment(sketch, "E7.11.12.1", {"start": v(26.79, 60.08) * mm, "end": v(29.03, 62.32) * mm});
            skLineSegment(sketch, "E7.11.12.3", {"start": v(29.03, 62.32) * mm, "end": v(30.26, 62.32) * mm});
            skLineSegment(sketch, "E7.11.12.4", {"start": v(32.2, 54.66) * mm, "end": v(34.45, 56.9) * mm});
            skLineSegment(sketch, "E7.11.12.5", {"start": v(34.45, 56.9) * mm, "end": v(34.45, 59.5) * mm});
            skLineSegment(sketch, "E7.11.12.6", {"start": v(26.79, 56.9) * mm, "end": v(29.03, 54.66) * mm});
            skLineSegment(sketch, "E7.11.12.7", {"start": v(26.79, 56.9) * mm, "end": v(26.79, 60.08) * mm});
            skLineSegment(sketch, "E7.12.0.1", {"start": v(35.68, -61.84) * mm, "end": v(37.92, -59.6) * mm});
            skLineSegment(sketch, "E7.12.0.2", {"start": v(41.1, -59.6) * mm, "end": v(43.34, -61.84) * mm});
            skLineSegment(sketch, "E7.12.0.3", {"start": v(37.92, -59.6) * mm, "end": v(41.1, -59.6) * mm});
            skLineSegment(sketch, "E7.12.1.0", {"start": v(37.92, -57.1) * mm, "end": v(41.1, -57.1) * mm});
            skLineSegment(sketch, "E7.12.1.1", {"start": v(35.68, -51.68) * mm, "end": v(37.92, -49.44) * mm});
            skLineSegment(sketch, "E7.12.1.2", {"start": v(41.1, -49.44) * mm, "end": v(43.34, -51.68) * mm});
            skLineSegment(sketch, "E7.12.1.3", {"start": v(37.92, -49.44) * mm, "end": v(41.1, -49.44) * mm});
            skLineSegment(sketch, "E7.12.1.4", {"start": v(41.1, -57.1) * mm, "end": v(43.34, -54.86) * mm});
            skLineSegment(sketch, "E7.12.1.5", {"start": v(43.34, -54.86) * mm, "end": v(43.34, -51.68) * mm});
            skLineSegment(sketch, "E7.12.1.6", {"start": v(35.68, -54.86) * mm, "end": v(37.92, -57.1) * mm});
            skLineSegment(sketch, "E7.12.1.7", {"start": v(35.68, -54.86) * mm, "end": v(35.68, -51.68) * mm});
            skLineSegment(sketch, "E7.12.2.0", {"start": v(37.92, -46.94) * mm, "end": v(41.1, -46.94) * mm});
            skLineSegment(sketch, "E7.12.2.1", {"start": v(35.68, -41.52) * mm, "end": v(37.92, -39.28) * mm});
            skLineSegment(sketch, "E7.12.2.2", {"start": v(41.1, -39.28) * mm, "end": v(43.34, -41.52) * mm});
            skLineSegment(sketch, "E7.12.2.3", {"start": v(37.92, -39.28) * mm, "end": v(41.1, -39.28) * mm});
            skLineSegment(sketch, "E7.12.2.4", {"start": v(41.1, -46.94) * mm, "end": v(43.34, -44.7) * mm});
            skLineSegment(sketch, "E7.12.2.5", {"start": v(43.34, -44.7) * mm, "end": v(43.34, -41.52) * mm});
            skLineSegment(sketch, "E7.12.2.6", {"start": v(35.68, -44.7) * mm, "end": v(37.92, -46.94) * mm});
            skLineSegment(sketch, "E7.12.2.7", {"start": v(35.68, -44.7) * mm, "end": v(35.68, -41.52) * mm});
            skLineSegment(sketch, "E7.12.3.0", {"start": v(37.92, -36.78) * mm, "end": v(41.1, -36.78) * mm});
            skLineSegment(sketch, "E7.12.3.1", {"start": v(35.68, -31.36) * mm, "end": v(37.92, -29.12) * mm});
            skLineSegment(sketch, "E7.12.3.2", {"start": v(41.1, -29.12) * mm, "end": v(43.34, -31.36) * mm});
            skLineSegment(sketch, "E7.12.3.3", {"start": v(37.92, -29.12) * mm, "end": v(41.1, -29.12) * mm});
            skLineSegment(sketch, "E7.12.3.4", {"start": v(41.1, -36.78) * mm, "end": v(43.34, -34.54) * mm});
            skLineSegment(sketch, "E7.12.3.5", {"start": v(43.34, -34.54) * mm, "end": v(43.34, -31.36) * mm});
            skLineSegment(sketch, "E7.12.3.6", {"start": v(35.68, -34.54) * mm, "end": v(37.92, -36.78) * mm});
            skLineSegment(sketch, "E7.12.3.7", {"start": v(35.68, -34.54) * mm, "end": v(35.68, -31.36) * mm});
            skLineSegment(sketch, "E7.12.4.0", {"start": v(37.92, -26.62) * mm, "end": v(41.1, -26.62) * mm});
            skLineSegment(sketch, "E7.12.4.1", {"start": v(35.68, -21.2) * mm, "end": v(37.92, -18.96) * mm});
            skLineSegment(sketch, "E7.12.4.2", {"start": v(41.1, -18.96) * mm, "end": v(43.34, -21.2) * mm});
            skLineSegment(sketch, "E7.12.4.3", {"start": v(37.92, -18.96) * mm, "end": v(41.1, -18.96) * mm});
            skLineSegment(sketch, "E7.12.4.4", {"start": v(41.1, -26.62) * mm, "end": v(43.34, -24.38) * mm});
            skLineSegment(sketch, "E7.12.4.5", {"start": v(43.34, -24.38) * mm, "end": v(43.34, -21.2) * mm});
            skLineSegment(sketch, "E7.12.4.6", {"start": v(35.68, -24.38) * mm, "end": v(37.92, -26.62) * mm});
            skLineSegment(sketch, "E7.12.4.7", {"start": v(35.68, -24.38) * mm, "end": v(35.68, -21.2) * mm});
            skLineSegment(sketch, "E7.12.5.0", {"start": v(37.92, -16.46) * mm, "end": v(41.1, -16.46) * mm});
            skLineSegment(sketch, "E7.12.5.1", {"start": v(35.68, -11.04) * mm, "end": v(37.92, -8.8) * mm});
            skLineSegment(sketch, "E7.12.5.2", {"start": v(41.1, -8.8) * mm, "end": v(43.34, -11.04) * mm});
            skLineSegment(sketch, "E7.12.5.3", {"start": v(37.92, -8.8) * mm, "end": v(41.1, -8.8) * mm});
            skLineSegment(sketch, "E7.12.5.4", {"start": v(41.1, -16.46) * mm, "end": v(43.34, -14.22) * mm});
            skLineSegment(sketch, "E7.12.5.5", {"start": v(43.34, -14.22) * mm, "end": v(43.34, -11.04) * mm});
            skLineSegment(sketch, "E7.12.5.6", {"start": v(35.68, -14.22) * mm, "end": v(37.92, -16.46) * mm});
            skLineSegment(sketch, "E7.12.5.7", {"start": v(35.68, -14.22) * mm, "end": v(35.68, -11.04) * mm});
            skLineSegment(sketch, "E7.12.6.0", {"start": v(37.92, -6.3) * mm, "end": v(41.1, -6.3) * mm});
            skLineSegment(sketch, "E7.12.6.1", {"start": v(35.68, -0.88) * mm, "end": v(37.92, 1.36) * mm});
            skLineSegment(sketch, "E7.12.6.2", {"start": v(41.1, 1.36) * mm, "end": v(43.34, -0.88) * mm});
            skLineSegment(sketch, "E7.12.6.3", {"start": v(37.92, 1.36) * mm, "end": v(41.1, 1.36) * mm});
            skLineSegment(sketch, "E7.12.6.4", {"start": v(41.1, -6.3) * mm, "end": v(43.34, -4.06) * mm});
            skLineSegment(sketch, "E7.12.6.5", {"start": v(43.34, -4.06) * mm, "end": v(43.34, -0.88) * mm});
            skLineSegment(sketch, "E7.12.6.6", {"start": v(35.68, -4.06) * mm, "end": v(37.92, -6.3) * mm});
            skLineSegment(sketch, "E7.12.6.7", {"start": v(35.68, -4.06) * mm, "end": v(35.68, -0.88) * mm});
            skLineSegment(sketch, "E7.12.7.0", {"start": v(37.92, 3.86) * mm, "end": v(41.1, 3.86) * mm});
            skLineSegment(sketch, "E7.12.7.1", {"start": v(35.68, 9.28) * mm, "end": v(37.92, 11.52) * mm});
            skLineSegment(sketch, "E7.12.7.2", {"start": v(41.1, 11.52) * mm, "end": v(43.34, 9.28) * mm});
            skLineSegment(sketch, "E7.12.7.3", {"start": v(37.92, 11.52) * mm, "end": v(41.1, 11.52) * mm});
            skLineSegment(sketch, "E7.12.7.4", {"start": v(41.1, 3.86) * mm, "end": v(43.34, 6.1) * mm});
            skLineSegment(sketch, "E7.12.7.5", {"start": v(43.34, 6.1) * mm, "end": v(43.34, 9.28) * mm});
            skLineSegment(sketch, "E7.12.7.6", {"start": v(35.68, 6.1) * mm, "end": v(37.92, 3.86) * mm});
            skLineSegment(sketch, "E7.12.7.7", {"start": v(35.68, 6.1) * mm, "end": v(35.68, 9.28) * mm});
            skLineSegment(sketch, "E7.12.8.0", {"start": v(37.92, 14.02) * mm, "end": v(41.1, 14.02) * mm});
            skLineSegment(sketch, "E7.12.8.1", {"start": v(35.68, 19.44) * mm, "end": v(37.92, 21.68) * mm});
            skLineSegment(sketch, "E7.12.8.2", {"start": v(41.1, 21.68) * mm, "end": v(43.34, 19.44) * mm});
            skLineSegment(sketch, "E7.12.8.3", {"start": v(37.92, 21.68) * mm, "end": v(41.1, 21.68) * mm});
            skLineSegment(sketch, "E7.12.8.4", {"start": v(41.1, 14.02) * mm, "end": v(43.34, 16.26) * mm});
            skLineSegment(sketch, "E7.12.8.5", {"start": v(43.34, 16.26) * mm, "end": v(43.34, 19.44) * mm});
            skLineSegment(sketch, "E7.12.8.6", {"start": v(35.68, 16.26) * mm, "end": v(37.92, 14.02) * mm});
            skLineSegment(sketch, "E7.12.8.7", {"start": v(35.68, 16.26) * mm, "end": v(35.68, 19.44) * mm});
            skLineSegment(sketch, "E7.12.9.0", {"start": v(37.92, 24.18) * mm, "end": v(41.1, 24.18) * mm});
            skLineSegment(sketch, "E7.12.9.1", {"start": v(35.68, 29.6) * mm, "end": v(37.92, 31.84) * mm});
            skLineSegment(sketch, "E7.12.9.2", {"start": v(41.1, 31.84) * mm, "end": v(43.34, 29.6) * mm});
            skLineSegment(sketch, "E7.12.9.3", {"start": v(37.92, 31.84) * mm, "end": v(41.1, 31.84) * mm});
            skLineSegment(sketch, "E7.12.9.4", {"start": v(41.1, 24.18) * mm, "end": v(43.34, 26.42) * mm});
            skLineSegment(sketch, "E7.12.9.5", {"start": v(43.34, 26.42) * mm, "end": v(43.34, 29.6) * mm});
            skLineSegment(sketch, "E7.12.9.6", {"start": v(35.68, 26.42) * mm, "end": v(37.92, 24.18) * mm});
            skLineSegment(sketch, "E7.12.9.7", {"start": v(35.68, 26.42) * mm, "end": v(35.68, 29.6) * mm});
            skLineSegment(sketch, "E7.12.10.0", {"start": v(37.92, 34.34) * mm, "end": v(41.1, 34.34) * mm});
            skLineSegment(sketch, "E7.12.10.1", {"start": v(35.68, 39.76) * mm, "end": v(37.92, 42) * mm});
            skLineSegment(sketch, "E7.12.10.2", {"start": v(41.1, 42) * mm, "end": v(43.34, 39.76) * mm});
            skLineSegment(sketch, "E7.12.10.3", {"start": v(37.92, 42) * mm, "end": v(41.1, 42) * mm});
            skLineSegment(sketch, "E7.12.10.4", {"start": v(41.1, 34.34) * mm, "end": v(43.34, 36.58) * mm});
            skLineSegment(sketch, "E7.12.10.5", {"start": v(43.34, 36.58) * mm, "end": v(43.34, 39.76) * mm});
            skLineSegment(sketch, "E7.12.10.6", {"start": v(35.68, 36.58) * mm, "end": v(37.92, 34.34) * mm});
            skLineSegment(sketch, "E7.12.10.7", {"start": v(35.68, 36.58) * mm, "end": v(35.68, 39.76) * mm});
            skLineSegment(sketch, "E7.12.11.0", {"start": v(37.92, 44.5) * mm, "end": v(41.1, 44.5) * mm});
            skLineSegment(sketch, "E7.12.11.1", {"start": v(35.68, 49.92) * mm, "end": v(37.92, 52.16) * mm});
            skLineSegment(sketch, "E7.12.11.2", {"start": v(41.1, 52.16) * mm, "end": v(43.34, 49.92) * mm});
            skLineSegment(sketch, "E7.12.11.3", {"start": v(37.92, 52.16) * mm, "end": v(41.1, 52.16) * mm});
            skLineSegment(sketch, "E7.12.11.4", {"start": v(41.1, 44.5) * mm, "end": v(43.34, 46.74) * mm});
            skLineSegment(sketch, "E7.12.11.5", {"start": v(43.34, 46.74) * mm, "end": v(43.34, 49.92) * mm});
            skLineSegment(sketch, "E7.12.11.6", {"start": v(35.68, 46.74) * mm, "end": v(37.92, 44.5) * mm});
            skLineSegment(sketch, "E7.12.11.7", {"start": v(35.68, 46.74) * mm, "end": v(35.68, 49.92) * mm});
            skLineSegment(sketch, "E7.12.12.0", {"start": v(37.92, 54.66) * mm, "end": v(40.19, 54.66) * mm});
            skLineSegment(sketch, "E7.12.12.6", {"start": v(35.68, 56.9) * mm, "end": v(37.92, 54.66) * mm});
            skLineSegment(sketch, "E7.12.12.7", {"start": v(35.68, 56.9) * mm, "end": v(35.68, 58.57) * mm});
            skLineSegment(sketch, "E7.13.0.1", {"start": v(44.57, -61.84) * mm, "end": v(46.81, -59.6) * mm});
            skLineSegment(sketch, "E7.13.0.2", {"start": v(49.99, -59.6) * mm, "end": v(50.67, -60.28) * mm});
            skLineSegment(sketch, "E7.13.0.3", {"start": v(46.81, -59.6) * mm, "end": v(49.99, -59.6) * mm});
            skLineSegment(sketch, "E7.13.1.0", {"start": v(46.81, -57.1) * mm, "end": v(49.99, -57.1) * mm});
            skLineSegment(sketch, "E7.13.1.1", {"start": v(44.57, -51.68) * mm, "end": v(46.81, -49.44) * mm});
            skLineSegment(sketch, "E7.13.1.2", {"start": v(49.99, -49.44) * mm, "end": v(52.23, -51.68) * mm});
            skLineSegment(sketch, "E7.13.1.3", {"start": v(46.81, -49.44) * mm, "end": v(49.99, -49.44) * mm});
            skLineSegment(sketch, "E7.13.1.4", {"start": v(49.99, -57.1) * mm, "end": v(52.23, -54.86) * mm});
            skLineSegment(sketch, "E7.13.1.5", {"start": v(52.23, -54.86) * mm, "end": v(52.23, -51.68) * mm});
            skLineSegment(sketch, "E7.13.1.6", {"start": v(44.57, -54.86) * mm, "end": v(46.81, -57.1) * mm});
            skLineSegment(sketch, "E7.13.1.7", {"start": v(44.57, -54.86) * mm, "end": v(44.57, -51.68) * mm});
            skLineSegment(sketch, "E7.13.2.0", {"start": v(46.81, -46.94) * mm, "end": v(49.99, -46.94) * mm});
            skLineSegment(sketch, "E7.13.2.1", {"start": v(44.57, -41.52) * mm, "end": v(46.81, -39.28) * mm});
            skLineSegment(sketch, "E7.13.2.2", {"start": v(49.99, -39.28) * mm, "end": v(52.23, -41.52) * mm});
            skLineSegment(sketch, "E7.13.2.3", {"start": v(46.81, -39.28) * mm, "end": v(49.99, -39.28) * mm});
            skLineSegment(sketch, "E7.13.2.4", {"start": v(49.99, -46.94) * mm, "end": v(52.23, -44.7) * mm});
            skLineSegment(sketch, "E7.13.2.5", {"start": v(52.23, -44.7) * mm, "end": v(52.23, -41.52) * mm});
            skLineSegment(sketch, "E7.13.2.6", {"start": v(44.57, -44.7) * mm, "end": v(46.81, -46.94) * mm});
            skLineSegment(sketch, "E7.13.2.7", {"start": v(44.57, -44.7) * mm, "end": v(44.57, -41.52) * mm});
            skLineSegment(sketch, "E7.13.3.0", {"start": v(46.81, -36.78) * mm, "end": v(49.99, -36.78) * mm});
            skLineSegment(sketch, "E7.13.3.1", {"start": v(44.57, -31.36) * mm, "end": v(46.81, -29.12) * mm});
            skLineSegment(sketch, "E7.13.3.2", {"start": v(49.99, -29.12) * mm, "end": v(52.23, -31.36) * mm});
            skLineSegment(sketch, "E7.13.3.3", {"start": v(46.81, -29.12) * mm, "end": v(49.99, -29.12) * mm});
            skLineSegment(sketch, "E7.13.3.4", {"start": v(49.99, -36.78) * mm, "end": v(52.23, -34.54) * mm});
            skLineSegment(sketch, "E7.13.3.5", {"start": v(52.23, -34.54) * mm, "end": v(52.23, -31.36) * mm});
            skLineSegment(sketch, "E7.13.3.6", {"start": v(44.57, -34.54) * mm, "end": v(46.81, -36.78) * mm});
            skLineSegment(sketch, "E7.13.3.7", {"start": v(44.57, -34.54) * mm, "end": v(44.57, -31.36) * mm});
            skLineSegment(sketch, "E7.13.4.0", {"start": v(46.81, -26.62) * mm, "end": v(49.99, -26.62) * mm});
            skLineSegment(sketch, "E7.13.4.1", {"start": v(44.57, -21.2) * mm, "end": v(46.81, -18.96) * mm});
            skLineSegment(sketch, "E7.13.4.2", {"start": v(49.99, -18.96) * mm, "end": v(52.23, -21.2) * mm});
            skLineSegment(sketch, "E7.13.4.3", {"start": v(46.81, -18.96) * mm, "end": v(49.99, -18.96) * mm});
            skLineSegment(sketch, "E7.13.4.4", {"start": v(49.99, -26.62) * mm, "end": v(52.23, -24.38) * mm});
            skLineSegment(sketch, "E7.13.4.5", {"start": v(52.23, -24.38) * mm, "end": v(52.23, -21.2) * mm});
            skLineSegment(sketch, "E7.13.4.6", {"start": v(44.57, -24.38) * mm, "end": v(46.81, -26.62) * mm});
            skLineSegment(sketch, "E7.13.4.7", {"start": v(44.57, -24.38) * mm, "end": v(44.57, -21.2) * mm});
            skLineSegment(sketch, "E7.13.5.0", {"start": v(46.81, -16.46) * mm, "end": v(49.99, -16.46) * mm});
            skLineSegment(sketch, "E7.13.5.1", {"start": v(44.57, -11.04) * mm, "end": v(46.81, -8.8) * mm});
            skLineSegment(sketch, "E7.13.5.2", {"start": v(49.99, -8.8) * mm, "end": v(52.23, -11.04) * mm});
            skLineSegment(sketch, "E7.13.5.3", {"start": v(46.81, -8.8) * mm, "end": v(49.99, -8.8) * mm});
            skLineSegment(sketch, "E7.13.5.4", {"start": v(49.99, -16.46) * mm, "end": v(52.23, -14.22) * mm});
            skLineSegment(sketch, "E7.13.5.5", {"start": v(52.23, -14.22) * mm, "end": v(52.23, -11.04) * mm});
            skLineSegment(sketch, "E7.13.5.6", {"start": v(44.57, -14.22) * mm, "end": v(46.81, -16.46) * mm});
            skLineSegment(sketch, "E7.13.5.7", {"start": v(44.57, -14.22) * mm, "end": v(44.57, -11.04) * mm});
            skLineSegment(sketch, "E7.13.6.0", {"start": v(46.81, -6.3) * mm, "end": v(49.99, -6.3) * mm});
            skLineSegment(sketch, "E7.13.6.1", {"start": v(44.57, -0.88) * mm, "end": v(46.81, 1.36) * mm});
            skLineSegment(sketch, "E7.13.6.2", {"start": v(49.99, 1.36) * mm, "end": v(52.23, -0.88) * mm});
            skLineSegment(sketch, "E7.13.6.3", {"start": v(46.81, 1.36) * mm, "end": v(49.99, 1.36) * mm});
            skLineSegment(sketch, "E7.13.6.4", {"start": v(49.99, -6.3) * mm, "end": v(52.23, -4.06) * mm});
            skLineSegment(sketch, "E7.13.6.5", {"start": v(52.23, -4.06) * mm, "end": v(52.23, -0.88) * mm});
            skLineSegment(sketch, "E7.13.6.6", {"start": v(44.57, -4.06) * mm, "end": v(46.81, -6.3) * mm});
            skLineSegment(sketch, "E7.13.6.7", {"start": v(44.57, -4.06) * mm, "end": v(44.57, -0.88) * mm});
            skLineSegment(sketch, "E7.13.7.0", {"start": v(46.81, 3.86) * mm, "end": v(49.99, 3.86) * mm});
            skLineSegment(sketch, "E7.13.7.1", {"start": v(44.57, 9.28) * mm, "end": v(46.81, 11.52) * mm});
            skLineSegment(sketch, "E7.13.7.2", {"start": v(49.99, 11.52) * mm, "end": v(52.23, 9.28) * mm});
            skLineSegment(sketch, "E7.13.7.3", {"start": v(46.81, 11.52) * mm, "end": v(49.99, 11.52) * mm});
            skLineSegment(sketch, "E7.13.7.4", {"start": v(49.99, 3.86) * mm, "end": v(52.23, 6.1) * mm});
            skLineSegment(sketch, "E7.13.7.5", {"start": v(52.23, 6.1) * mm, "end": v(52.23, 9.28) * mm});
            skLineSegment(sketch, "E7.13.7.6", {"start": v(44.57, 6.1) * mm, "end": v(46.81, 3.86) * mm});
            skLineSegment(sketch, "E7.13.7.7", {"start": v(44.57, 6.1) * mm, "end": v(44.57, 9.28) * mm});
            skLineSegment(sketch, "E7.13.8.0", {"start": v(46.81, 14.02) * mm, "end": v(49.99, 14.02) * mm});
            skLineSegment(sketch, "E7.13.8.1", {"start": v(44.57, 19.44) * mm, "end": v(46.81, 21.68) * mm});
            skLineSegment(sketch, "E7.13.8.2", {"start": v(49.99, 21.68) * mm, "end": v(52.23, 19.44) * mm});
            skLineSegment(sketch, "E7.13.8.3", {"start": v(46.81, 21.68) * mm, "end": v(49.99, 21.68) * mm});
            skLineSegment(sketch, "E7.13.8.4", {"start": v(49.99, 14.02) * mm, "end": v(52.23, 16.26) * mm});
            skLineSegment(sketch, "E7.13.8.5", {"start": v(52.23, 16.26) * mm, "end": v(52.23, 19.44) * mm});
            skLineSegment(sketch, "E7.13.8.6", {"start": v(44.57, 16.26) * mm, "end": v(46.81, 14.02) * mm});
            skLineSegment(sketch, "E7.13.8.7", {"start": v(44.57, 16.26) * mm, "end": v(44.57, 19.44) * mm});
            skLineSegment(sketch, "E7.13.9.0", {"start": v(46.81, 24.18) * mm, "end": v(49.99, 24.18) * mm});
            skLineSegment(sketch, "E7.13.9.1", {"start": v(44.57, 29.6) * mm, "end": v(46.81, 31.84) * mm});
            skLineSegment(sketch, "E7.13.9.2", {"start": v(49.99, 31.84) * mm, "end": v(52.23, 29.6) * mm});
            skLineSegment(sketch, "E7.13.9.3", {"start": v(46.81, 31.84) * mm, "end": v(49.99, 31.84) * mm});
            skLineSegment(sketch, "E7.13.9.4", {"start": v(49.99, 24.18) * mm, "end": v(52.23, 26.42) * mm});
            skLineSegment(sketch, "E7.13.9.5", {"start": v(52.23, 26.42) * mm, "end": v(52.23, 29.6) * mm});
            skLineSegment(sketch, "E7.13.9.6", {"start": v(44.57, 26.42) * mm, "end": v(46.81, 24.18) * mm});
            skLineSegment(sketch, "E7.13.9.7", {"start": v(44.57, 26.42) * mm, "end": v(44.57, 29.6) * mm});
            skLineSegment(sketch, "E7.13.10.0", {"start": v(46.81, 34.34) * mm, "end": v(49.99, 34.34) * mm});
            skLineSegment(sketch, "E7.13.10.1", {"start": v(44.57, 39.76) * mm, "end": v(46.81, 42) * mm});
            skLineSegment(sketch, "E7.13.10.2", {"start": v(49.99, 42) * mm, "end": v(50.32, 41.67) * mm});
            skLineSegment(sketch, "E7.13.10.3", {"start": v(46.81, 42) * mm, "end": v(49.99, 42) * mm});
            skLineSegment(sketch, "E7.13.10.4", {"start": v(49.99, 34.34) * mm, "end": v(52.23, 36.58) * mm});
            skLineSegment(sketch, "E7.13.10.5", {"start": v(52.23, 36.58) * mm, "end": v(52.23, 38.04) * mm});
            skLineSegment(sketch, "E7.13.10.6", {"start": v(44.57, 36.58) * mm, "end": v(46.81, 34.34) * mm});
            skLineSegment(sketch, "E7.13.10.7", {"start": v(44.57, 36.58) * mm, "end": v(44.57, 39.76) * mm});
            skLineSegment(sketch, "E7.13.11.0", {"start": v(46.81, 44.5) * mm, "end": v(48.6, 44.5) * mm});
            skLineSegment(sketch, "E7.13.11.1", {"start": v(44.57, 49.92) * mm, "end": v(44.58, 49.94) * mm});
            skLineSegment(sketch, "E7.13.11.6", {"start": v(44.57, 46.74) * mm, "end": v(46.81, 44.5) * mm});
            skLineSegment(sketch, "E7.13.11.7", {"start": v(44.57, 46.74) * mm, "end": v(44.57, 49.92) * mm});
            skLineSegment(sketch, "E7.14.1.1", {"start": v(53.46, -51.68) * mm, "end": v(55.7, -49.44) * mm});
            skLineSegment(sketch, "E7.14.1.3", {"start": v(55.7, -49.44) * mm, "end": v(57.26, -49.44) * mm});
            skLineSegment(sketch, "E7.14.1.6", {"start": v(53.46, -54.86) * mm, "end": v(55, -56.4) * mm});
            skLineSegment(sketch, "E7.14.1.7", {"start": v(53.46, -54.86) * mm, "end": v(53.46, -51.68) * mm});
            skLineSegment(sketch, "E7.14.2.0", {"start": v(55.7, -46.94) * mm, "end": v(57.3, -46.94) * mm});
            skLineSegment(sketch, "E7.14.2.1", {"start": v(53.46, -41.52) * mm, "end": v(55.7, -39.28) * mm});
            skLineSegment(sketch, "E7.14.2.3", {"start": v(55.7, -39.28) * mm, "end": v(57.38, -39.28) * mm});
            skLineSegment(sketch, "E7.14.2.6", {"start": v(53.46, -44.7) * mm, "end": v(55.7, -46.94) * mm});
            skLineSegment(sketch, "E7.14.2.7", {"start": v(53.46, -44.7) * mm, "end": v(53.46, -41.52) * mm});
            skLineSegment(sketch, "E7.14.3.0", {"start": v(55.7, -36.78) * mm, "end": v(57.41, -36.78) * mm});
            skLineSegment(sketch, "E7.14.3.1", {"start": v(53.46, -31.36) * mm, "end": v(55.7, -29.12) * mm});
            skLineSegment(sketch, "E7.14.3.3", {"start": v(55.7, -29.12) * mm, "end": v(57.5, -29.12) * mm});
            skLineSegment(sketch, "E7.14.3.6", {"start": v(53.46, -34.54) * mm, "end": v(55.7, -36.78) * mm});
            skLineSegment(sketch, "E7.14.3.7", {"start": v(53.46, -34.54) * mm, "end": v(53.46, -31.36) * mm});
            skLineSegment(sketch, "E7.14.4.0", {"start": v(55.7, -26.62) * mm, "end": v(57.53, -26.62) * mm});
            skLineSegment(sketch, "E7.14.4.1", {"start": v(53.46, -21.2) * mm, "end": v(55.7, -18.96) * mm});
            skLineSegment(sketch, "E7.14.4.3", {"start": v(55.7, -18.96) * mm, "end": v(57.62, -18.96) * mm});
            skLineSegment(sketch, "E7.14.4.6", {"start": v(53.46, -24.38) * mm, "end": v(55.7, -26.62) * mm});
            skLineSegment(sketch, "E7.14.4.7", {"start": v(53.46, -24.38) * mm, "end": v(53.46, -21.2) * mm});
            skLineSegment(sketch, "E7.14.5.0", {"start": v(55.7, -16.46) * mm, "end": v(57.64, -16.46) * mm});
            skLineSegment(sketch, "E7.14.5.1", {"start": v(53.46, -11.04) * mm, "end": v(55.7, -8.8) * mm});
            skLineSegment(sketch, "E7.14.5.3", {"start": v(55.7, -8.8) * mm, "end": v(57.73, -8.8) * mm});
            skLineSegment(sketch, "E7.14.5.6", {"start": v(53.46, -14.22) * mm, "end": v(55.7, -16.46) * mm});
            skLineSegment(sketch, "E7.14.5.7", {"start": v(53.46, -14.22) * mm, "end": v(53.46, -11.04) * mm});
            skLineSegment(sketch, "E7.14.6.0", {"start": v(55.7, -6.3) * mm, "end": v(57.76, -6.3) * mm});
            skLineSegment(sketch, "E7.14.6.1", {"start": v(53.46, -0.88) * mm, "end": v(55.7, 1.36) * mm});
            skLineSegment(sketch, "E7.14.6.3", {"start": v(55.7, 1.36) * mm, "end": v(57.85, 1.36) * mm});
            skLineSegment(sketch, "E7.14.6.6", {"start": v(53.46, -4.06) * mm, "end": v(55.7, -6.3) * mm});
            skLineSegment(sketch, "E7.14.6.7", {"start": v(53.46, -4.06) * mm, "end": v(53.46, -0.88) * mm});
            skLineSegment(sketch, "E7.14.7.0", {"start": v(55.7, 3.86) * mm, "end": v(57.88, 3.86) * mm});
            skLineSegment(sketch, "E7.14.7.1", {"start": v(53.46, 9.28) * mm, "end": v(55.7, 11.52) * mm});
            skLineSegment(sketch, "E7.14.7.3", {"start": v(55.7, 11.52) * mm, "end": v(57.97, 11.52) * mm});
            skLineSegment(sketch, "E7.14.7.6", {"start": v(53.46, 6.1) * mm, "end": v(55.7, 3.86) * mm});
            skLineSegment(sketch, "E7.14.7.7", {"start": v(53.46, 6.1) * mm, "end": v(53.46, 9.28) * mm});
            skLineSegment(sketch, "E7.14.8.0", {"start": v(55.7, 14.02) * mm, "end": v(57.97, 14.02) * mm});
            skLineSegment(sketch, "E7.14.8.1", {"start": v(53.46, 19.44) * mm, "end": v(55.7, 21.68) * mm});
            skLineSegment(sketch, "E7.14.8.3", {"start": v(55.7, 21.68) * mm, "end": v(57.3, 21.68) * mm});
            skLineSegment(sketch, "E7.14.8.6", {"start": v(53.46, 16.26) * mm, "end": v(55.7, 14.02) * mm});
            skLineSegment(sketch, "E7.14.8.7", {"start": v(53.46, 16.26) * mm, "end": v(53.46, 19.44) * mm});
            skLineSegment(sketch, "E7.14.9.0", {"start": v(55.7, 24.18) * mm, "end": v(56.87, 24.18) * mm});
            skLineSegment(sketch, "E7.14.9.1", {"start": v(53.46, 29.6) * mm, "end": v(55.02, 31.16) * mm});
            skLineSegment(sketch, "E7.14.9.6", {"start": v(53.46, 26.42) * mm, "end": v(55.7, 24.18) * mm});
            skLineSegment(sketch, "E7.14.9.7", {"start": v(53.46, 26.42) * mm, "end": v(53.46, 29.6) * mm});
            skArc(sketch, "E8", {"start": v(57.97, 14.02) * mm, "mid": v(57.77, 17.86) * mm, "end": v(57.3, 21.68) * mm});
            skArc(sketch, "E9.filletArc", {"start": v(44.57, -61.84) * mm, "mid": v(47.72, -61.44) * mm, "end": v(50.67, -60.28) * mm});
            skPoint(sketch, "E10.endSnap0", {"position": v(-20.46, 98.22) * mm});
            skLineSegment(sketch, "E11.0", {"start": v(-38.76, -61.84) * mm, "end": v(-36.67, -61.84) * mm});
            skLineSegment(sketch, "E12", {"start": v(-57.85, 11.52) * mm, "end": v(-57.05, 3.86) * mm});
            skLineSegment(sketch, "E13", {"start": v(57.97, 11.52) * mm, "end": v(57.88, 3.86) * mm});
            skArc(sketch, "E14.filletArc", {"start": v(-51.39, -50.46) * mm, "mid": v(-50.5, -53.98) * mm, "end": v(-48.65, -57.1) * mm});
            skLineSegment(sketch, "E15", {"start": v(-8.77, 67.06) * mm, "end": v(-8.77, 70.18) * mm});
            skArc(sketch, "E16.trimOffspring", {"start": v(-30.27, 62.32) * mm, "mid": v(-32.9, 60.61) * mm, "end": v(-35.44, 58.76) * mm});
            skArc(sketch, "E17.trimOffspring", {"start": v(-18.89, 67.7) * mm, "mid": v(-21.87, 66.57) * mm, "end": v(-24.78, 65.3) * mm});
            skArc(sketch, "E18.trimOffspring", {"start": v(-10, 69.98) * mm, "mid": v(-13.86, 69.17) * mm, "end": v(-17.66, 68.1) * mm});
            skLineSegment(sketch, "E19.trimOffspring", {"start": v(-35.44, -61.84) * mm, "end": v(-27.78, -61.84) * mm});
            skLineSegment(sketch, "E20.trimOffspring", {"start": v(-26.55, -61.84) * mm, "end": v(-18.89, -61.84) * mm});
            skLineSegment(sketch, "E21.trimOffspring", {"start": v(-17.66, -61.84) * mm, "end": v(-10, -61.84) * mm});
            skLineSegment(sketch, "E22.trimOffspring", {"start": v(-8.77, -61.84) * mm, "end": v(-1.1, -61.84) * mm});
            skLineSegment(sketch, "E23.trimOffspring", {"start": v(0.12, -61.84) * mm, "end": v(7.78, -61.84) * mm});
            skLineSegment(sketch, "E24.trimOffspring", {"start": v(9, -61.84) * mm, "end": v(16.67, -61.84) * mm});
            skLineSegment(sketch, "E25.trimOffspring", {"start": v(17.9, -61.84) * mm, "end": v(25.56, -61.84) * mm});
            skLineSegment(sketch, "E26.trimOffspring", {"start": v(26.79, -61.84) * mm, "end": v(34.45, -61.84) * mm});
            skLineSegment(sketch, "E27.trimOffspring", {"start": v(35.68, -61.84) * mm, "end": v(43.34, -61.84) * mm});
            skArc(sketch, "E28.trimOffspring", {"start": v(55, -56.4) * mm, "mid": v(56.66, -53) * mm, "end": v(57.27, -49.29) * mm});
            skLineSegment(sketch, "E29.trimOffspring", {"start": v(57.38, -39.28) * mm, "end": v(57.3, -46.94) * mm});
            skLineSegment(sketch, "E30.trimOffspring", {"start": v(57.5, -29.12) * mm, "end": v(57.41, -36.78) * mm});
            skLineSegment(sketch, "E31.trimOffspring", {"start": v(57.62, -18.96) * mm, "end": v(57.53, -26.62) * mm});
            skLineSegment(sketch, "E32.trimOffspring", {"start": v(57.85, 1.36) * mm, "end": v(57.64, -16.46) * mm});
            skArc(sketch, "E33.trimOffspring", {"start": v(52.23, 38.04) * mm, "mid": v(51.3, 39.87) * mm, "end": v(50.32, 41.67) * mm});
            skArc(sketch, "E34.trimOffspring", {"start": v(48.6, 44.5) * mm, "mid": v(46.67, 47.28) * mm, "end": v(44.58, 49.94) * mm});
            skArc(sketch, "E35.trimOffspring", {"start": v(40.19, 54.66) * mm, "mid": v(37.98, 56.67) * mm, "end": v(35.68, 58.57) * mm});
            skArc(sketch, "E36.trimOffspring", {"start": v(34.45, 59.5) * mm, "mid": v(32.39, 60.96) * mm, "end": v(30.26, 62.32) * mm});
            skArc(sketch, "E37.trimOffspring", {"start": v(24.1, 65.6) * mm, "mid": v(21.03, 66.9) * mm, "end": v(17.9, 68.02) * mm});
            skArc(sketch, "E38.trimOffspring", {"start": v(16.67, 68.4) * mm, "mid": v(12.87, 69.4) * mm, "end": v(9, 70.15) * mm});
            skArc(sketch, "E39.trimOffspring", {"start": v(7.68, 70.34) * mm, "mid": v(4.21, 70.7) * mm, "end": v(0.72, 70.85) * mm});
            skArc(sketch, "E40.trimOffspring", {"start": v(-1.7, 70.83) * mm, "mid": v(-5.24, 70.61) * mm, "end": v(-8.77, 70.18) * mm});
            skArc(sketch, "E41.trimOffspring", {"start": v(-43.44, -60.95) * mm, "mid": v(-41.14, -61.61) * mm, "end": v(-38.76, -61.84) * mm});
            skLineSegment(sketch, "E42.trimOffspring", {"start": v(-51.45, -49.9) * mm, "end": v(-51.39, -50.46) * mm});
            skLineSegment(sketch, "E43.trimOffspring", {"start": v(-52.4, -40.7) * mm, "end": v(-51.84, -46.07) * mm});
            skLineSegment(sketch, "E44.trimOffspring", {"start": v(-53.22, -32.86) * mm, "end": v(-53.03, -34.73) * mm});
            skLineSegment(sketch, "E45.trimOffspring", {"start": v(-55.62, -9.87) * mm, "end": v(-55.1, -14.87) * mm});
            skLineSegment(sketch, "E46.trimOffspring", {"start": v(-56.8, 1.36) * mm, "end": v(-56.06, -5.67) * mm});
            skArc(sketch, "E47.trimOffspring", {"start": v(-57.32, 21.68) * mm, "mid": v(-57.78, 17.86) * mm, "end": v(-57.98, 14.02) * mm});
            skArc(sketch, "E48.trimOffspring", {"start": v(-55.27, 30.42) * mm, "mid": v(-56.16, 27.32) * mm, "end": v(-56.88, 24.18) * mm});
            skArc(sketch, "E49.trimOffspring", {"start": v(-50.14, 42) * mm, "mid": v(-51.65, 39.23) * mm, "end": v(-53.01, 36.37) * mm});
            skArc(sketch, "E50.trimOffspring", {"start": v(-45.56, 48.74) * mm, "mid": v(-47.13, 46.66) * mm, "end": v(-48.6, 44.5) * mm});
            skArc(sketch, "E51.trimOffspring", {"start": v(-36.67, 57.79) * mm, "mid": v(-38.47, 56.26) * mm, "end": v(-40.2, 54.66) * mm});
            skSolve(sketch);
        }
        {
            var Q0;
            Q0=makeQuery(id+"F2.imprint","IMPRINT",FACE,{"disambiguationData":[TD([[makeQuery(id+"F2.imprint","IMPRINT",EDGE,{"derivedFrom":sQuery(id+"F2.wireOp",EDGE,"E7.1.5.2")}),1.0]])]});
            extrude(context, id + "F3", {"entities" : qUnion([Q0]), "operationType" : NewBodyOperationType.ADD, "depth" : 8.9 * mm, "offsetDistance" : 25.4 * mm});
        }
    });
